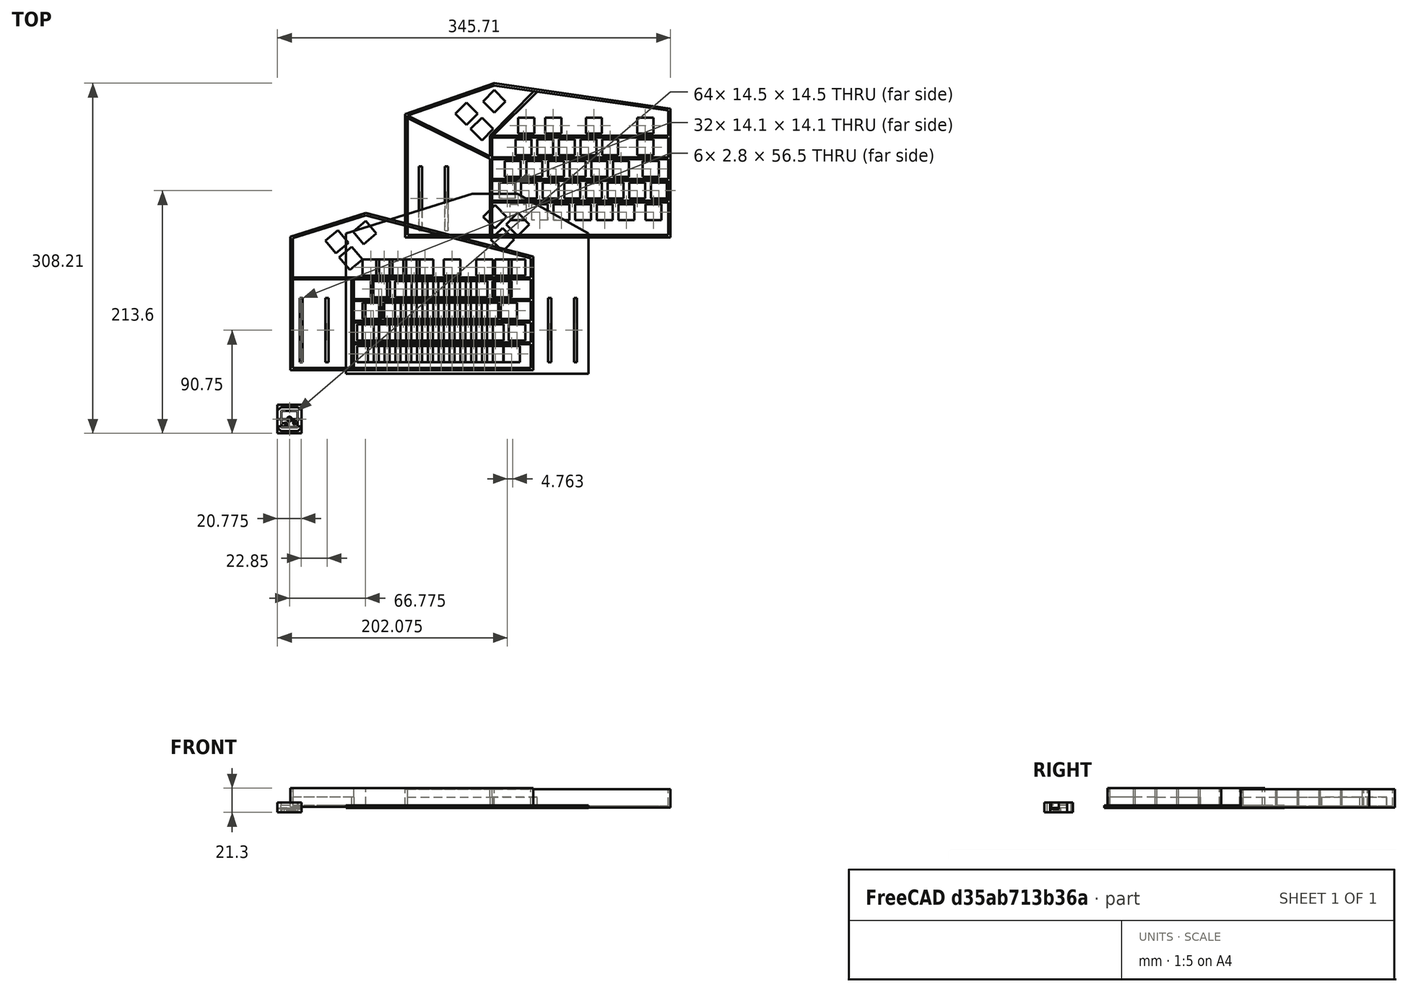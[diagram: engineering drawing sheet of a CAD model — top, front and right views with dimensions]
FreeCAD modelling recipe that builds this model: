
FCSTD DOCUMENT  (FreeCAD 0.22R35869 (Git))
Label: keyboard.FCStd.bak
License: All rights reserved
LicenseURL: http://en.wikipedia.org/wiki/All_rights_reserved
objects: Sketcher::SketchObject×30, PartDesign::Pad×30, PartDesign::Pocket×25, PartDesign::CoordinateSystem×11, PartDesign::Body×7, Part::Feature×6, App::Part×4, App::DocumentObjectGroup×3, App::Link×3, Mesh::Feature×3, Part::Refine×3, PartDesign::FeatureBase×3, PartDesign::Chamfer×2, PartDesign::Fillet×2, PartDesign::LinearPattern×2, App::FeaturePython×1, Spreadsheet::Sheet×1
note: 180 computed .brp shape members not serialized (recipe doc carries the construction recipe); baked Part::Feature solids carry a one-line shape summary decoded from their .brp

FEATURE [Sketcher::SketchObject] Sketch
  FullyConstrained = true
  MapMode = 5
  Support = -> [XY_Plane001]
  sketch-geometry (8):
    g0: LineSegment StartX=-7.5 StartY=7.5 StartZ=0 EndX=7.5 EndY=7.5 EndZ=0
    g1: LineSegment StartX=7.5 StartY=7.5 StartZ=0 EndX=7.5 EndY=-7.5 EndZ=0
    g2: LineSegment StartX=7.5 StartY=-7.5 StartZ=0 EndX=-7.5 EndY=-7.5 EndZ=0
    g3: LineSegment StartX=-7.5 StartY=-7.5 StartZ=0 EndX=-7.5 EndY=7.5 EndZ=0
    g4: LineSegment StartX=-10.5 StartY=10.5 StartZ=0 EndX=10.5 EndY=10.5 EndZ=0
    g5: LineSegment StartX=10.5 StartY=10.5 StartZ=0 EndX=10.5 EndY=-10.5 EndZ=0
    g6: LineSegment StartX=10.5 StartY=-10.5 StartZ=0 EndX=-10.5 EndY=-10.5 EndZ=0
    g7: LineSegment StartX=-10.5 StartY=-10.5 StartZ=0 EndX=-10.5 EndY=10.5 EndZ=0
  constraints (20):
    c: Coincident(g0,g1)
    c: Coincident(g1,g2)
    c: Coincident(g2,g3)
    c: Coincident(g3,g0)
    c: Horizontal(g2)
    c: Vertical(g1)
    c: Symmetric(g0,g0,g-2)
    c: Symmetric(g0,g2,g-1)
    c: Equal(g0,g3)
    c: DistanceX(g0,g0) = 15
    c: Coincident(g4,g5)
    c: Coincident(g5,g6)
    c: Coincident(g6,g7)
    c: Coincident(g7,g4)
    c: Horizontal(g6)
    c: Vertical(g5)
    c: Symmetric(g4,g4,g-2)
    c: Symmetric(g4,g6,g-1)
    c: Equal(g4,g7)
    c: DistanceX(g4,g0) = 3
FEATURE [PartDesign::Pad] Pad
  Direction = (0,0,1)
  Length = 2.5
  Length2 = 10
  Profile = -> Sketch
  ReferenceAxis = -> Sketch [N_Axis]
  Type = 0
FEATURE [Sketcher::SketchObject] Sketch001
  ExternalGeometry = -> [Pad]
  FullyConstrained = true
  MapMode = 5
  Placement = pos=(0,0,0) rot=(1,0,0;3.14159rad)
  Support = -> [Pad]
  expr: Constraints[11] = 4.15 / 2
  sketch-geometry (5):
    g0: LineSegment StartX=-10.5 StartY=10.5 StartZ=0 EndX=10.5 EndY=10.5 EndZ=0
    g1: LineSegment StartX=10.5 StartY=10.5 StartZ=0 EndX=10.5 EndY=-10.5 EndZ=0
    g2: LineSegment StartX=10.5 StartY=-10.5 StartZ=0 EndX=-10.5 EndY=-10.5 EndZ=0
    g3: LineSegment StartX=-10.5 StartY=-10.5 StartZ=0 EndX=-10.5 EndY=10.5 EndZ=0
    g4: Circle CenterX=0 CenterY=0 CenterZ=0 NormalX=0 NormalY=0 NormalZ=1 AngleXU=0 Radius=2.075
  constraints (12):
    c: Coincident(g0,g1)
    c: Coincident(g1,g2)
    c: Coincident(g2,g3)
    c: Coincident(g3,g0)
    c: Horizontal(g0)
    c: Horizontal(g2)
    c: Vertical(g1)
    c: Vertical(g3)
    c: Coincident(g0,g-3)
    c: Coincident(g1,g-4)
    c: Coincident(g4,g-1)
    c: Radius(g4) = 2.075
FEATURE [PartDesign::Pad] Pad001
  BaseFeature = -> Pad
  Direction = (0,0,-1)
  Length = 4
  Length2 = 10
  Profile = -> Sketch001
  ReferenceAxis = -> Sketch001 [N_Axis]
  Type = 0
FEATURE [Sketcher::SketchObject] Sketch002
  ExternalGeometry = -> [Pad001]
  FullyConstrained = true
  MapMode = 5
  Placement = pos=(0,0,2.5) rot=(0,0,1;0rad)
  Support = -> [Pad001]
  sketch-geometry (8):
    g0: LineSegment StartX=-10.5 StartY=10.5 StartZ=0 EndX=10.5 EndY=10.5 EndZ=0
    g1: LineSegment StartX=10.5 StartY=10.5 StartZ=0 EndX=10.5 EndY=-10.5 EndZ=0
    g2: LineSegment StartX=10.5 StartY=-10.5 StartZ=0 EndX=-10.5 EndY=-10.5 EndZ=0
    g3: LineSegment StartX=-10.5 StartY=-10.5 StartZ=0 EndX=-10.5 EndY=10.5 EndZ=0
    g4: LineSegment StartX=-7.25 StartY=7.25 StartZ=0 EndX=7.25 EndY=7.25 EndZ=0
    g5: LineSegment StartX=7.25 StartY=7.25 StartZ=0 EndX=7.25 EndY=-7.25 EndZ=0
    g6: LineSegment StartX=7.25 StartY=-7.25 StartZ=0 EndX=-7.25 EndY=-7.25 EndZ=0
    g7: LineSegment StartX=-7.25 StartY=-7.25 StartZ=0 EndX=-7.25 EndY=7.25 EndZ=0
  constraints (20):
    c: Coincident(g0,g1)
    c: Coincident(g1,g2)
    c: Coincident(g2,g3)
    c: Coincident(g3,g0)
    c: Horizontal(g0)
    c: Horizontal(g2)
    c: Vertical(g1)
    c: Vertical(g3)
    c: Coincident(g0,g-3)
    c: Coincident(g1,g-4)
    c: Coincident(g4,g5)
    c: Coincident(g5,g6)
    c: Coincident(g6,g7)
    c: Coincident(g7,g4)
    c: Horizontal(g6)
    c: Vertical(g5)
    c: Symmetric(g4,g4,g-2)
    c: Symmetric(g4,g6,g-1)
    c: DistanceX(g4,g4) = 14.5
    c: Equal(g7,g4)
FEATURE [PartDesign::Pad] Pad002
  BaseFeature = -> Pad001
  Direction = (0,0,1)
  Length = 2.3
  Length2 = 10
  Profile = -> Sketch002
  ReferenceAxis = -> Sketch002 [N_Axis]
  Type = 0
FEATURE [PartDesign::Chamfer] Chamfer
  Angle = 45
  Base = -> Pad002 [Edge19,Edge23,Edge11,Edge12]
  BaseFeature = -> Pad002
  ChamferType = 0
  FlipDirection = false
  Size = 3
  Size2 = 1
  SupportTransform = false
  UseAllEdges = false
FEATURE [Sketcher::SketchObject] Sketch003
  FullyConstrained = true
  MapMode = 5
  Placement = pos=(0,0,-4) rot=(1,0,0;3.14159rad)
  Support = -> [Chamfer]
  sketch-geometry (2):
    g0: Circle CenterX=4 CenterY=2.85 CenterZ=0 NormalX=0 NormalY=0 NormalZ=1 AngleXU=0 Radius=0.75
    g1: Circle CenterX=-2.9 CenterY=5 CenterZ=0 NormalX=0 NormalY=0 NormalZ=1 AngleXU=0 Radius=0.75
  constraints (6):
    c: DistanceX(g-1,g0) = 4
    c: DistanceY(g-1,g0) = 2.85
    c: Radius(g0) = 0.75
    c: DistanceX(g1,g-1) = 2.9
    c: DistanceY(g-1,g1) = 5
    c: Equal(g1,g0)
FEATURE [PartDesign::Pocket] Pocket
  BaseFeature = -> Chamfer
  Direction = (0,0,1)
  Length = 5
  Length2 = 5
  Profile = -> Sketch003
  ReferenceAxis = -> Sketch003 [N_Axis]
  Type = 1
FEATURE [PartDesign::Chamfer] Chamfer001
  Angle = 45
  Base = -> Pocket [Edge27,Edge26]
  BaseFeature = -> Pocket
  ChamferType = 1
  FlipDirection = false
  Size = 1.8
  Size2 = 3.999
  SupportTransform = false
  UseAllEdges = false
FEATURE [PartDesign::Body] Body
  Group = -> [Sketch,Pad,Sketch001,Pad001,Sketch002,Pad002,Chamfer,Sketch003,Pocket,Chamfer001]
  Origin = -> Origin001
  Tip = -> Chamfer001
FEATURE [Sketcher::SketchObject] Sketch004
  FullyConstrained = true
  MapMode = 5
  Support = -> [XY_Plane002]
  sketch-geometry (8):
    g0: LineSegment StartX=-7.5 StartY=7.5 StartZ=0 EndX=7.5 EndY=7.5 EndZ=0
    g1: LineSegment StartX=7.5 StartY=7.5 StartZ=0 EndX=7.5 EndY=-7.5 EndZ=0
    g2: LineSegment StartX=7.5 StartY=-7.5 StartZ=0 EndX=-7.5 EndY=-7.5 EndZ=0
    g3: LineSegment StartX=-7.5 StartY=-7.5 StartZ=0 EndX=-7.5 EndY=7.5 EndZ=0
    g4: LineSegment StartX=-10.5 StartY=10.5 StartZ=0 EndX=10.5 EndY=10.5 EndZ=0
    g5: LineSegment StartX=10.5 StartY=10.5 StartZ=0 EndX=10.5 EndY=-10.5 EndZ=0
    g6: LineSegment StartX=10.5 StartY=-10.5 StartZ=0 EndX=-10.5 EndY=-10.5 EndZ=0
    g7: LineSegment StartX=-10.5 StartY=-10.5 StartZ=0 EndX=-10.5 EndY=10.5 EndZ=0
  constraints (20):
    c: Coincident(g0,g1)
    c: Coincident(g1,g2)
    c: Coincident(g2,g3)
    c: Coincident(g3,g0)
    c: Horizontal(g2)
    c: Vertical(g1)
    c: Symmetric(g0,g0,g-2)
    c: Symmetric(g0,g2,g-1)
    c: Equal(g0,g3)
    c: DistanceX(g0,g0) = 15
    c: Coincident(g4,g5)
    c: Coincident(g5,g6)
    c: Coincident(g6,g7)
    c: Coincident(g7,g4)
    c: Horizontal(g6)
    c: Vertical(g5)
    c: Symmetric(g4,g4,g-2)
    c: Symmetric(g4,g6,g-1)
    c: Equal(g4,g7)
    c: DistanceX(g4,g0) = 3
FEATURE [PartDesign::Pad] Pad003
  Direction = (0,0,1)
  Length = 2.5
  Length2 = 10
  Profile = -> Sketch004
  ReferenceAxis = -> Sketch004 [N_Axis]
  Type = 0
FEATURE [Sketcher::SketchObject] Sketch005
  ExternalGeometry = -> [Pad003]
  FullyConstrained = true
  MapMode = 5
  Placement = pos=(0,0,0) rot=(1,0,0;3.14159rad)
  Support = -> [Pad003]
  expr: Constraints[11] = 4.15 / 2
  sketch-geometry (5):
    g0: LineSegment StartX=-10.5 StartY=10.5 StartZ=0 EndX=10.5 EndY=10.5 EndZ=0
    g1: LineSegment StartX=10.5 StartY=10.5 StartZ=0 EndX=10.5 EndY=-10.5 EndZ=0
    g2: LineSegment StartX=10.5 StartY=-10.5 StartZ=0 EndX=-10.5 EndY=-10.5 EndZ=0
    g3: LineSegment StartX=-10.5 StartY=-10.5 StartZ=0 EndX=-10.5 EndY=10.5 EndZ=0
    g4: Circle CenterX=0 CenterY=0 CenterZ=0 NormalX=0 NormalY=0 NormalZ=1 AngleXU=0 Radius=2.075
  constraints (12):
    c: Coincident(g0,g1)
    c: Coincident(g1,g2)
    c: Coincident(g2,g3)
    c: Coincident(g3,g0)
    c: Horizontal(g0)
    c: Horizontal(g2)
    c: Vertical(g1)
    c: Vertical(g3)
    c: Coincident(g0,g-3)
    c: Coincident(g1,g-4)
    c: Coincident(g4,g-1)
    c: Radius(g4) = 2.075
FEATURE [PartDesign::Pad] Pad004
  BaseFeature = -> Pad003
  Direction = (0,0,-1)
  Length = 4
  Length2 = 10
  Profile = -> Sketch005
  ReferenceAxis = -> Sketch005 [N_Axis]
  Type = 0
FEATURE [Sketcher::SketchObject] Sketch006
  ExternalGeometry = -> [Pad004]
  FullyConstrained = true
  MapMode = 5
  Placement = pos=(0,0,2.5) rot=(0,0,1;0rad)
  Support = -> [Pad004]
  sketch-geometry (8):
    g0: LineSegment StartX=-10.5 StartY=10.5 StartZ=0 EndX=10.5 EndY=10.5 EndZ=0
    g1: LineSegment StartX=10.5 StartY=10.5 StartZ=0 EndX=10.5 EndY=-10.5 EndZ=0
    g2: LineSegment StartX=10.5 StartY=-10.5 StartZ=0 EndX=-10.5 EndY=-10.5 EndZ=0
    g3: LineSegment StartX=-10.5 StartY=-10.5 StartZ=0 EndX=-10.5 EndY=10.5 EndZ=0
    g4: LineSegment StartX=-7.25 StartY=7.25 StartZ=0 EndX=7.25 EndY=7.25 EndZ=0
    g5: LineSegment StartX=7.25 StartY=7.25 StartZ=0 EndX=7.25 EndY=-7.25 EndZ=0
    g6: LineSegment StartX=7.25 StartY=-7.25 StartZ=0 EndX=-7.25 EndY=-7.25 EndZ=0
    g7: LineSegment StartX=-7.25 StartY=-7.25 StartZ=0 EndX=-7.25 EndY=7.25 EndZ=0
  constraints (20):
    c: Coincident(g0,g1)
    c: Coincident(g1,g2)
    c: Coincident(g2,g3)
    c: Coincident(g3,g0)
    c: Horizontal(g0)
    c: Horizontal(g2)
    c: Vertical(g1)
    c: Vertical(g3)
    c: Coincident(g0,g-3)
    c: Coincident(g1,g-4)
    c: Coincident(g4,g5)
    c: Coincident(g5,g6)
    c: Coincident(g6,g7)
    c: Coincident(g7,g4)
    c: Horizontal(g6)
    c: Vertical(g5)
    c: Symmetric(g4,g4,g-2)
    c: Symmetric(g4,g6,g-1)
    c: DistanceX(g4,g4) = 14.5
    c: Equal(g7,g4)
FEATURE [PartDesign::Pad] Pad005
  BaseFeature = -> Pad004
  Direction = (0,0,1)
  Length = 2.3
  Length2 = 10
  Profile = -> Sketch006
  ReferenceAxis = -> Sketch006 [N_Axis]
  Type = 0
FEATURE [Sketcher::SketchObject] Sketch007
  ExternalGeometry = -> [Pad005]
  FullyConstrained = true
  MapMode = 5
  Placement = pos=(0,0,-4) rot=(1,0,0;3.14159rad)
  Support = -> [Pad005]
  sketch-geometry (22):
    g0: LineSegment StartX=-7.5 StartY=6.5 StartZ=0 EndX=-2 EndY=6.5 EndZ=0
    g1: LineSegment StartX=-2 StartY=6.5 StartZ=0 EndX=-2 EndY=3.5 EndZ=0
    g2: LineSegment StartX=-2 StartY=3.5 StartZ=0 EndX=-7.5 EndY=3.5 EndZ=0
    g3: LineSegment StartX=-7.5 StartY=3.5 StartZ=0 EndX=-7.5 EndY=6.5 EndZ=0
    g4: LineSegment StartX=3 StartY=4.35 StartZ=0 EndX=7.5 EndY=4.35 EndZ=0
    g5: LineSegment StartX=7.5 StartY=4.35 StartZ=0 EndX=7.5 EndY=1.35 EndZ=0
    g6: LineSegment StartX=7.5 StartY=1.35 StartZ=0 EndX=3 EndY=1.35 EndZ=0
    g7: LineSegment StartX=3 StartY=1.35 StartZ=0 EndX=3 EndY=4.35 EndZ=0
    g8: Circle CenterX=-2.9 CenterY=5 CenterZ=0 NormalX=0 NormalY=0 NormalZ=1 AngleXU=0 Radius=0.75
    g9: Circle CenterX=4 CenterY=2.85 CenterZ=0 NormalX=0 NormalY=0 NormalZ=1 AngleXU=0 Radius=0.75
    g10: LineSegment StartX=-2.9 StartY=5 StartZ=0 EndX=-7.5 EndY=5 EndZ=0
    g11: LineSegment StartX=-7.5 StartY=5 StartZ=0 EndX=-7.5 EndY=6.5 EndZ=0
    g12: LineSegment StartX=-7.5 StartY=5 StartZ=0 EndX=-7.5 EndY=3.5 EndZ=0
    g13: LineSegment StartX=4 StartY=2.85 StartZ=0 EndX=7.5 EndY=2.85 EndZ=0
    g14: LineSegment StartX=7.5 StartY=2.85 StartZ=0 EndX=7.5 EndY=1.35 EndZ=0
    g15: LineSegment StartX=7.5 StartY=2.85 StartZ=0 EndX=7.5 EndY=4.35 EndZ=0
    g16: LineSegment StartX=3 StartY=4.35 StartZ=0 EndX=3.8 EndY=3.57284 EndZ=0
    g17: LineSegment StartX=3 StartY=1.35 StartZ=0 EndX=3.8 EndY=2.12716 EndZ=0
    g18: ArcOfCircle CenterX=4 CenterY=2.85 CenterZ=0 NormalX=0 NormalY=0 NormalZ=1 AngleXU=0 Radius=0.75 StartAngle=1.84073 EndAngle=4.44246
    g19: LineSegment StartX=-2 StartY=6.5 StartZ=0 EndX=-2.7 EndY=5.72284 EndZ=0
    g20: LineSegment StartX=-2 StartY=3.5 StartZ=0 EndX=-2.7 EndY=4.27716 EndZ=0
    g21: ArcOfCircle CenterX=-2.9 CenterY=5 CenterZ=0 NormalX=0 NormalY=0 NormalZ=1 AngleXU=0 Radius=0.75 StartAngle=4.98232 EndAngle=7.58405
  constraints (60):
    c: Coincident(g0,g1)
    c: Coincident(g1,g2)
    c: Coincident(g2,g3)
    c: Coincident(g3,g0)
    c: Horizontal(g0)
    c: Horizontal(g2)
    c: Vertical(g1)
    c: Vertical(g3)
    c: Coincident(g4,g5)
    c: Coincident(g5,g6)
    c: Coincident(g6,g7)
    c: Coincident(g7,g4)
    c: Horizontal(g4)
    c: Horizontal(g6)
    c: Vertical(g5)
    c: Vertical(g7)
    c: PointOnObject(g4,g-4)
    c: PointOnObject(g0,g-3)
    c: DistanceY(g-1,g9) = 2.85
    c: DistanceX(g-1,g9) = 4
    c: Radius(g9) = 0.75
    c: DistanceY(g-1,g8) = 5
    c: DistanceX(g8,g-1) = 2.9
    c: Radius(g8) = 0.75
    c: Coincident(g10,g8)
    c: PointOnObject(g10,g-3)
    c: Coincident(g11,g10)
    c: Equal(g12,g11)
    c: Coincident(g12,g10)
    c: Horizontal(g10)
    c: Coincident(g12,g2)
    c: Coincident(g11,g0)
    c: Coincident(g13,g9)
    c: PointOnObject(g13,g-4)
    c: Coincident(g14,g13)
    c: Coincident(g15,g13)
    c: Equal(g15,g14)
    c: Horizontal(g13)
    c: Coincident(g15,g4)
    c: Coincident(g14,g5)
    c: DistanceX(g6,g5) = 4.5
    c: DistanceX(g2,g2) = 5.5
    c: DistanceY(g1,g1) = 3
    c: Coincident(g16,g4)
    c: Coincident(g17,g6)
    c: Coincident(g18,g9)
    c: Coincident(g18,g16)
    c: Coincident(g18,g17)
    c: Equal(g18,g9)
    c: DistanceX(g17,g18) = 0.2
    c: Equal(g16,g17)
    c: Coincident(g19,g0)
    c: PointOnObject(g19,g8)
    c: Coincident(g20,g2)
    c: Coincident(g21,g8)
    c: Coincident(g21,g19)
    c: Coincident(g21,g20)
    c: Equal(g19,g20)
    c: DistanceX(g21,g20) = 0.2
    c: Equal(g1,g7)
FEATURE [PartDesign::Pocket] Pocket001
  BaseFeature = -> Pad005
  Direction = (0,0,1)
  Length = 0
  Length2 = 5
  Profile = -> Sketch007
  ReferenceAxis = -> Sketch007 [N_Axis]
  Type = 3
  UpToFace = -> Pad005 [Face20]
FEATURE [PartDesign::Fillet] Fillet
  Base = -> Pocket001 [Edge65,Edge68,Edge49,Edge53]
  BaseFeature = -> Pocket001
  Radius = 1
  SupportTransform = false
  UseAllEdges = false
FEATURE [Sketcher::SketchObject] Sketch008
  ExternalGeometry = -> [Fillet]
  FullyConstrained = true
  MapMode = 5
  Placement = pos=(0,0,4.8) rot=(0,0,1;0rad)
  Support = -> [Fillet]
  sketch-geometry (4):
    g0: LineSegment StartX=-10.5 StartY=0 StartZ=0 EndX=10.5 EndY=0 EndZ=0
    g1: LineSegment StartX=10.5 StartY=0 StartZ=0 EndX=10.5 EndY=-6.5 EndZ=0
    g2: LineSegment StartX=10.5 StartY=-6.5 StartZ=0 EndX=-10.5 EndY=-6.5 EndZ=0
    g3: LineSegment StartX=-10.5 StartY=-6.5 StartZ=0 EndX=-10.5 EndY=0 EndZ=0
  constraints (11):
    c: Coincident(g0,g1)
    c: Coincident(g1,g2)
    c: Coincident(g2,g3)
    c: Coincident(g3,g0)
    c: Horizontal(g2)
    c: Vertical(g1)
    c: Vertical(g3)
    c: PointOnObject(g0,g-1)
    c: PointOnObject(g2,g-3)
    c: Symmetric(g0,g0,g-2)
    c: PointOnObject(g2,g-4)
FEATURE [PartDesign::Pocket] Pocket002
  BaseFeature = -> Fillet
  Direction = (0,0,-1)
  Length = 0
  Length2 = 5
  Profile = -> Sketch008
  ReferenceAxis = -> Sketch008 [N_Axis]
  Type = 3
  UpToFace = -> Fillet [Face23]
FEATURE [PartDesign::Pad] Pad006
  BaseFeature = -> Pocket002
  Direction = (0,-1,0)
  Length = 2
  Length2 = 10
  Profile = -> Pocket002 [Face10,Face26,Face39]
  Type = 0
FEATURE [PartDesign::Pad] Pad007
  BaseFeature = -> Pad006
  Direction = (0,1,0)
  Length = 2
  Length2 = 10
  Profile = -> Pad006 [Face13,Face34,Face50]
  Type = 0
FEATURE [PartDesign::CoordinateSystem] LCS_Origin
  AttacherType = Attacher::AttachEngine3D
  MapMode = 2
  Support = -> [X_Axis006]
FEATURE [App::DocumentObjectGroup] Constraints
FEATURE [App::FeaturePython] Variables  # WARN: FeaturePython — macro-defined, semantics opaque (R4)
  Type = App::PropertyContainer
FEATURE [App::DocumentObjectGroup] Configurations
FEATURE [PartDesign::CoordinateSystem] LCS_0
  AttacherType = Attacher::AttachEngine3D
  MapMode = 2
  Support = -> [X_Axis007]
FEATURE [Sketcher::SketchObject] Sketch013
  FullyConstrained = true
  MapMode = 5
  Support = -> [XY_Plane008]
  sketch-geometry (6):
    g0: ArcOfCircle CenterX=-0.866025 CenterY=0 CenterZ=0 NormalX=0 NormalY=0 NormalZ=1 AngleXU=0 Radius=1 StartAngle=5.75959 EndAngle=6.80678
    g1: LineSegment StartX=0 StartY=0.5 StartZ=0 EndX=0 EndY=1 EndZ=0
    g2: LineSegment StartX=0 StartY=1 StartZ=0 EndX=1 EndY=1 EndZ=0
    g3: LineSegment StartX=1 StartY=1 StartZ=0 EndX=1 EndY=-1 EndZ=0
    g4: LineSegment StartX=1 StartY=-1 StartZ=0 EndX=0 EndY=-1 EndZ=0
    g5: LineSegment StartX=0 StartY=-1 StartZ=0 EndX=2e-16 EndY=-0.5 EndZ=0
  constraints (19):
    c: PointOnObject(g0,g-1)
    c: PointOnObject(g0,g-2)
    c: PointOnObject(g0,g-2)
    c: Coincident(g1,g2)
    c: Horizontal(g2)
    c: Coincident(g2,g3)
    c: Coincident(g3,g4)
    c: PointOnObject(g4,g-2)
    c: Horizontal(g4)
    c: Coincident(g4,g5)
    c: Coincident(g5,g0)
    c: PointOnObject(g1,g-2)
    c: Vertical(g3)
    c: DistanceY(g3,g3) = 2
    c: Radius(g0) = 1
    c: Coincident(g1,g0)
    c: Equal(g1,g5)
    c: DistanceY(g0,g0) = 1
    c: DistanceX(g2,g2) = 1
FEATURE [PartDesign::Pad] Pad011
  Direction = (0,0,1)
  Length = 4
  Length2 = 10
  Profile = -> Sketch013
  ReferenceAxis = -> Sketch013 [N_Axis]
  Reversed = true
  Type = 0
FEATURE [PartDesign::CoordinateSystem] Local_CS
  AttacherType = Attacher::AttachEngine3D
  MapMode = 45
  Placement = pos=(3.31163,-2.85,0) rot=(0,0.707107,0.707107;3.14159rad)
  Support = -> [Pad007]
FEATURE [PartDesign::CoordinateSystem] Local_CS001
  AttacherType = Attacher::AttachEngine3D
  MapMode = 45
  Placement = pos=(-2.22398,-5,0) rot=(0,0.707107,0.707107;3.14159rad)
  Support = -> [Pad007]
FEATURE [PartDesign::Body] Body001
  Group = -> [Sketch004,Pad003,Sketch005,Pad004,Sketch006,Pad005,Sketch007,Pocket001,Fillet,Sketch008,Pocket002,Pad006,Pad007,Local_CS,Local_CS001]
  Origin = -> Origin002
  Tip = -> Pad007
FEATURE [Sketcher::SketchObject] Sketch014
  ExternalGeometry = -> [Pad011]
  FullyConstrained = true
  MapMode = 5
  Support = -> [XY_Plane008]
  sketch-geometry (21):
    g0: LineSegment StartX=1 StartY=1 StartZ=0 EndX=1.66667 EndY=-0.8 EndZ=0
    g1: LineSegment StartX=1.66667 StartY=-0.8 StartZ=0 EndX=2.33333 EndY=1 EndZ=0
    g2: LineSegment StartX=2.33333 StartY=1 StartZ=0 EndX=3 EndY=-0.8 EndZ=0
    g3: LineSegment StartX=3 StartY=-0.8 StartZ=0 EndX=3.66667 EndY=1 EndZ=0
    g4: LineSegment StartX=3.66667 StartY=1 StartZ=0 EndX=4.33333 EndY=-0.8 EndZ=0
    g5: LineSegment StartX=4.33333 StartY=-0.8 StartZ=0 EndX=5 EndY=1 EndZ=0
    g6: LineSegment StartX=1 StartY=1 StartZ=0 EndX=5 EndY=1 EndZ=0
    g7: LineSegment StartX=1 StartY=-1 StartZ=0 EndX=4.33333 EndY=-1 EndZ=0
    g8: LineSegment StartX=1 StartY=0.8 StartZ=0 EndX=1.66667 EndY=-1 EndZ=0
    g9: LineSegment StartX=1.66667 StartY=-1 StartZ=0 EndX=2.33333 EndY=0.8 EndZ=0
    g10: LineSegment StartX=2.33333 StartY=0.8 StartZ=0 EndX=3 EndY=-1 EndZ=0
    g11: LineSegment StartX=3 StartY=-1 StartZ=0 EndX=3.66667 EndY=0.8 EndZ=0
    g12: LineSegment StartX=3.66667 StartY=0.8 StartZ=0 EndX=4.33333 EndY=-1 EndZ=0
    g13: LineSegment StartX=4.33333 StartY=-1 StartZ=0 EndX=5 EndY=0.8 EndZ=0
    g14: LineSegment StartX=1.66667 StartY=-0.8 StartZ=0 EndX=1.66667 EndY=-1 EndZ=0
    g15: LineSegment StartX=3 StartY=-0.8 StartZ=0 EndX=3 EndY=-1 EndZ=0
    g16: LineSegment StartX=2.33333 StartY=0.8 StartZ=0 EndX=2.33333 EndY=1 EndZ=0
    g17: LineSegment StartX=3.66667 StartY=0.8 StartZ=0 EndX=3.66667 EndY=1 EndZ=0
    g18: LineSegment StartX=5 StartY=0.8 StartZ=0 EndX=5 EndY=1 EndZ=0
    g19: LineSegment StartX=4.33333 StartY=-0.8 StartZ=0 EndX=4.33333 EndY=-1 EndZ=0
    g20: LineSegment StartX=1 StartY=0.8 StartZ=0 EndX=1 EndY=1 EndZ=0
  constraints (55):
    c: Coincident(g-3,g0)
    c: Coincident(g0,g1)
    c: Coincident(g1,g2)
    c: Coincident(g2,g3)
    c: Coincident(g3,g4)
    c: Coincident(g6,g0)
    c: Coincident(g6,g5)
    c: Coincident(g7,g-3)
    c: Horizontal(g7)
    c: Horizontal(g6)
    c: PointOnObject(g3,g6)
    c: PointOnObject(g1,g6)
    c: Coincident(g5,g4)
    c: PointOnObject(g8,g-3)
    c: PointOnObject(g8,g7)
    c: Coincident(g8,g9)
    c: Coincident(g9,g10)
    c: PointOnObject(g10,g7)
    c: Coincident(g10,g11)
    c: Coincident(g11,g12)
    c: Coincident(g12,g7)
    c: Coincident(g12,g13)
    c: Coincident(g14,g0)
    c: Coincident(g14,g8)
    c: Coincident(g15,g2)
    c: Coincident(g15,g10)
    c: Coincident(g16,g9)
    c: Coincident(g16,g1)
    c: Coincident(g17,g11)
    c: Coincident(g17,g3)
    c: Vertical(g17)
    c: Coincident(g18,g13)
    c: Coincident(g18,g5)
    c: Coincident(g19,g4)
    c: Coincident(g19,g12)
    c: Equal(g14,g16)
    c: Equal(g16,g15)
    c: Equal(g15,g17)
    c: Equal(g17,g19)
    c: Equal(g19,g18)
    c: Vertical(g14)
    c: Vertical(g16)
    c: Vertical(g15)
    c: Vertical(g18)
    c: Vertical(g19)
    c: Equal(g0,g1)
    c: Equal(g2,g3)
    c: Equal(g3,g4)
    c: Equal(g4,g5)
    c: Equal(g5,g8)
    c: Equal(g8,g9)
    c: Coincident(g20,g8)
    c: Coincident(g20,g0)
    c: DistanceY(g18,g18) = 0.2
    c: DistanceX(g6,g6) = 4
FEATURE [PartDesign::Pad] Pad012
  BaseFeature = -> Pad011
  Direction = (0,0,1)
  Length = 4
  Length2 = 10
  Profile = -> Sketch014
  ReferenceAxis = -> Sketch014 [N_Axis]
  Reversed = true
  Type = 0
FEATURE [PartDesign::CoordinateSystem] LCS_0002
  AttacherType = Attacher::AttachEngine3D
  MapMode = 2
  Support = -> [X_Axis009]
FEATURE [Sketcher::SketchObject] Sketch015
  FullyConstrained = true
  MapMode = 5
  Support = -> [XY_Plane010]
  sketch-geometry (8):
    g0: LineSegment StartX=-7.5 StartY=7.5 StartZ=0 EndX=7.5 EndY=7.5 EndZ=0
    g1: LineSegment StartX=7.5 StartY=7.5 StartZ=0 EndX=7.5 EndY=-7.5 EndZ=0
    g2: LineSegment StartX=7.5 StartY=-7.5 StartZ=0 EndX=-7.5 EndY=-7.5 EndZ=0
    g3: LineSegment StartX=-7.5 StartY=-7.5 StartZ=0 EndX=-7.5 EndY=7.5 EndZ=0
    g4: LineSegment StartX=-10.5 StartY=10.5 StartZ=0 EndX=10.5 EndY=10.5 EndZ=0
    g5: LineSegment StartX=10.5 StartY=10.5 StartZ=0 EndX=10.5 EndY=-10.5 EndZ=0
    g6: LineSegment StartX=10.5 StartY=-10.5 StartZ=0 EndX=-10.5 EndY=-10.5 EndZ=0
    g7: LineSegment StartX=-10.5 StartY=-10.5 StartZ=0 EndX=-10.5 EndY=10.5 EndZ=0
  constraints (20):
    c: Coincident(g0,g1)
    c: Coincident(g1,g2)
    c: Coincident(g2,g3)
    c: Coincident(g3,g0)
    c: Horizontal(g2)
    c: Vertical(g1)
    c: Symmetric(g0,g0,g-2)
    c: Symmetric(g0,g2,g-1)
    c: Equal(g0,g3)
    c: DistanceX(g0,g0) = 15
    c: Coincident(g4,g5)
    c: Coincident(g5,g6)
    c: Coincident(g6,g7)
    c: Coincident(g7,g4)
    c: Horizontal(g6)
    c: Vertical(g5)
    c: Symmetric(g4,g4,g-2)
    c: Symmetric(g4,g6,g-1)
    c: Equal(g4,g7)
    c: DistanceX(g4,g0) = 3
FEATURE [PartDesign::Pad] Pad013
  Direction = (0,0,1)
  Length = 2.5
  Length2 = 10
  Profile = -> Sketch015
  ReferenceAxis = -> Sketch015 [N_Axis]
  Type = 0
FEATURE [Sketcher::SketchObject] Sketch016
  ExternalGeometry = -> [Pad013]
  FullyConstrained = true
  MapMode = 5
  Placement = pos=(0,0,0) rot=(1,0,0;3.14159rad)
  Support = -> [Pad013]
  expr: Constraints[11] = 4.15 / 2
  sketch-geometry (5):
    g0: LineSegment StartX=-10.5 StartY=10.5 StartZ=0 EndX=10.5 EndY=10.5 EndZ=0
    g1: LineSegment StartX=10.5 StartY=10.5 StartZ=0 EndX=10.5 EndY=-10.5 EndZ=0
    g2: LineSegment StartX=10.5 StartY=-10.5 StartZ=0 EndX=-10.5 EndY=-10.5 EndZ=0
    g3: LineSegment StartX=-10.5 StartY=-10.5 StartZ=0 EndX=-10.5 EndY=10.5 EndZ=0
    g4: Circle CenterX=0 CenterY=0 CenterZ=0 NormalX=0 NormalY=0 NormalZ=1 AngleXU=0 Radius=2.075
  constraints (12):
    c: Coincident(g0,g1)
    c: Coincident(g1,g2)
    c: Coincident(g2,g3)
    c: Coincident(g3,g0)
    c: Horizontal(g0)
    c: Horizontal(g2)
    c: Vertical(g1)
    c: Vertical(g3)
    c: Coincident(g0,g-3)
    c: Coincident(g1,g-4)
    c: Coincident(g4,g-1)
    c: Radius(g4) = 2.075
FEATURE [PartDesign::Pad] Pad014
  BaseFeature = -> Pad013
  Direction = (0,0,-1)
  Length = 4
  Length2 = 10
  Profile = -> Sketch016
  ReferenceAxis = -> Sketch016 [N_Axis]
  Type = 0
FEATURE [Sketcher::SketchObject] Sketch017
  ExternalGeometry = -> [Pad014]
  FullyConstrained = true
  MapMode = 5
  Placement = pos=(0,0,2.5) rot=(0,0,1;0rad)
  Support = -> [Pad014]
  sketch-geometry (8):
    g0: LineSegment StartX=-10.5 StartY=10.5 StartZ=0 EndX=10.5 EndY=10.5 EndZ=0
    g1: LineSegment StartX=10.5 StartY=10.5 StartZ=0 EndX=10.5 EndY=-10.5 EndZ=0
    g2: LineSegment StartX=10.5 StartY=-10.5 StartZ=0 EndX=-10.5 EndY=-10.5 EndZ=0
    g3: LineSegment StartX=-10.5 StartY=-10.5 StartZ=0 EndX=-10.5 EndY=10.5 EndZ=0
    g4: LineSegment StartX=-7.25 StartY=7.25 StartZ=0 EndX=7.25 EndY=7.25 EndZ=0
    g5: LineSegment StartX=7.25 StartY=7.25 StartZ=0 EndX=7.25 EndY=-7.25 EndZ=0
    g6: LineSegment StartX=7.25 StartY=-7.25 StartZ=0 EndX=-7.25 EndY=-7.25 EndZ=0
    g7: LineSegment StartX=-7.25 StartY=-7.25 StartZ=0 EndX=-7.25 EndY=7.25 EndZ=0
  constraints (20):
    c: Coincident(g0,g1)
    c: Coincident(g1,g2)
    c: Coincident(g2,g3)
    c: Coincident(g3,g0)
    c: Horizontal(g0)
    c: Horizontal(g2)
    c: Vertical(g1)
    c: Vertical(g3)
    c: Coincident(g0,g-3)
    c: Coincident(g1,g-4)
    c: Coincident(g4,g5)
    c: Coincident(g5,g6)
    c: Coincident(g6,g7)
    c: Coincident(g7,g4)
    c: Horizontal(g6)
    c: Vertical(g5)
    c: Symmetric(g4,g4,g-2)
    c: Symmetric(g4,g6,g-1)
    c: DistanceX(g4,g4) = 14.5
    c: Equal(g7,g4)
FEATURE [PartDesign::Pad] Pad015
  BaseFeature = -> Pad014
  Direction = (0,0,1)
  Length = 2.3
  Length2 = 10
  Profile = -> Sketch017
  ReferenceAxis = -> Sketch017 [N_Axis]
  Type = 0
FEATURE [Sketcher::SketchObject] Sketch018
  ExternalGeometry = -> [Pad015]
  FullyConstrained = true
  MapMode = 5
  Placement = pos=(0,0,-4) rot=(1,0,0;3.14159rad)
  Support = -> [Pad015]
  sketch-geometry (22):
    g0: LineSegment StartX=-7.5 StartY=6.5 StartZ=0 EndX=-2 EndY=6.5 EndZ=0
    g1: LineSegment StartX=-2 StartY=6.5 StartZ=0 EndX=-2 EndY=3.5 EndZ=0
    g2: LineSegment StartX=-2 StartY=3.5 StartZ=0 EndX=-7.5 EndY=3.5 EndZ=0
    g3: LineSegment StartX=-7.5 StartY=3.5 StartZ=0 EndX=-7.5 EndY=6.5 EndZ=0
    g4: LineSegment StartX=3 StartY=4.35 StartZ=0 EndX=7.5 EndY=4.35 EndZ=0
    g5: LineSegment StartX=7.5 StartY=4.35 StartZ=0 EndX=7.5 EndY=1.35 EndZ=0
    g6: LineSegment StartX=7.5 StartY=1.35 StartZ=0 EndX=3 EndY=1.35 EndZ=0
    g7: LineSegment StartX=3 StartY=1.35 StartZ=0 EndX=3 EndY=4.35 EndZ=0
    g8: Circle CenterX=-2.9 CenterY=5 CenterZ=0 NormalX=0 NormalY=0 NormalZ=1 AngleXU=0 Radius=0.75
    g9: Circle CenterX=4 CenterY=2.85 CenterZ=0 NormalX=0 NormalY=0 NormalZ=1 AngleXU=0 Radius=0.75
    g10: LineSegment StartX=-2.9 StartY=5 StartZ=0 EndX=-7.5 EndY=5 EndZ=0
    g11: LineSegment StartX=-7.5 StartY=5 StartZ=0 EndX=-7.5 EndY=6.5 EndZ=0
    g12: LineSegment StartX=-7.5 StartY=5 StartZ=0 EndX=-7.5 EndY=3.5 EndZ=0
    g13: LineSegment StartX=4 StartY=2.85 StartZ=0 EndX=7.5 EndY=2.85 EndZ=0
    g14: LineSegment StartX=7.5 StartY=2.85 StartZ=0 EndX=7.5 EndY=1.35 EndZ=0
    g15: LineSegment StartX=7.5 StartY=2.85 StartZ=0 EndX=7.5 EndY=4.35 EndZ=0
    g16: LineSegment StartX=3 StartY=4.35 StartZ=0 EndX=3.8 EndY=3.57284 EndZ=0
    g17: LineSegment StartX=3 StartY=1.35 StartZ=0 EndX=3.8 EndY=2.12716 EndZ=0
    g18: ArcOfCircle CenterX=4 CenterY=2.85 CenterZ=0 NormalX=0 NormalY=0 NormalZ=1 AngleXU=0 Radius=0.75 StartAngle=1.84073 EndAngle=4.44246
    g19: LineSegment StartX=-2 StartY=6.5 StartZ=0 EndX=-2.7 EndY=5.72284 EndZ=0
    g20: LineSegment StartX=-2 StartY=3.5 StartZ=0 EndX=-2.7 EndY=4.27716 EndZ=0
    g21: ArcOfCircle CenterX=-2.9 CenterY=5 CenterZ=0 NormalX=0 NormalY=0 NormalZ=1 AngleXU=0 Radius=0.75 StartAngle=4.98232 EndAngle=7.58405
  constraints (60):
    c: Coincident(g0,g1)
    c: Coincident(g1,g2)
    c: Coincident(g2,g3)
    c: Coincident(g3,g0)
    c: Horizontal(g0)
    c: Horizontal(g2)
    c: Vertical(g1)
    c: Vertical(g3)
    c: Coincident(g4,g5)
    c: Coincident(g5,g6)
    c: Coincident(g6,g7)
    c: Coincident(g7,g4)
    c: Horizontal(g4)
    c: Horizontal(g6)
    c: Vertical(g5)
    c: Vertical(g7)
    c: PointOnObject(g4,g-4)
    c: PointOnObject(g0,g-3)
    c: DistanceY(g-1,g9) = 2.85
    c: DistanceX(g-1,g9) = 4
    c: Radius(g9) = 0.75
    c: DistanceY(g-1,g8) = 5
    c: DistanceX(g8,g-1) = 2.9
    c: Radius(g8) = 0.75
    c: Coincident(g10,g8)
    c: PointOnObject(g10,g-3)
    c: Coincident(g11,g10)
    c: Equal(g12,g11)
    c: Coincident(g12,g10)
    c: Horizontal(g10)
    c: Coincident(g12,g2)
    c: Coincident(g11,g0)
    c: Coincident(g13,g9)
    c: PointOnObject(g13,g-4)
    c: Coincident(g14,g13)
    c: Coincident(g15,g13)
    c: Equal(g15,g14)
    c: Horizontal(g13)
    c: Coincident(g15,g4)
    c: Coincident(g14,g5)
    c: DistanceX(g6,g5) = 4.5
    c: DistanceX(g2,g2) = 5.5
    c: DistanceY(g1,g1) = 3
    c: Coincident(g16,g4)
    c: Coincident(g17,g6)
    c: Coincident(g18,g9)
    c: Coincident(g18,g16)
    c: Coincident(g18,g17)
    c: Equal(g18,g9)
    c: DistanceX(g17,g18) = 0.2
    c: Equal(g16,g17)
    c: Coincident(g19,g0)
    c: PointOnObject(g19,g8)
    c: Coincident(g20,g2)
    c: Coincident(g21,g8)
    c: Coincident(g21,g19)
    c: Coincident(g21,g20)
    c: Equal(g19,g20)
    c: DistanceX(g21,g20) = 0.2
    c: Equal(g1,g7)
FEATURE [PartDesign::Pocket] Pocket003
  BaseFeature = -> Pad015
  Direction = (0,0,1)
  Length = 0
  Length2 = 5
  Profile = -> Sketch018
  ReferenceAxis = -> Sketch018 [N_Axis]
  Type = 3
  UpToFace = -> Pad015 [Face20]
FEATURE [PartDesign::Fillet] Fillet001
  Base = -> Pocket003 [Edge65,Edge68,Edge49,Edge53]
  BaseFeature = -> Pocket003
  Radius = 1
  SupportTransform = false
  UseAllEdges = false
FEATURE [Sketcher::SketchObject] Sketch019
  ExternalGeometry = -> [Fillet001]
  FullyConstrained = true
  MapMode = 5
  Placement = pos=(0,0,4.8) rot=(0,0,1;0rad)
  Support = -> [Fillet001]
  sketch-geometry (4):
    g0: LineSegment StartX=-10.5 StartY=0 StartZ=0 EndX=10.5 EndY=0 EndZ=0
    g1: LineSegment StartX=10.5 StartY=0 StartZ=0 EndX=10.5 EndY=-6.5 EndZ=0
    g2: LineSegment StartX=10.5 StartY=-6.5 StartZ=0 EndX=-10.5 EndY=-6.5 EndZ=0
    g3: LineSegment StartX=-10.5 StartY=-6.5 StartZ=0 EndX=-10.5 EndY=0 EndZ=0
  constraints (11):
    c: Coincident(g0,g1)
    c: Coincident(g1,g2)
    c: Coincident(g2,g3)
    c: Coincident(g3,g0)
    c: Horizontal(g2)
    c: Vertical(g1)
    c: Vertical(g3)
    c: PointOnObject(g0,g-1)
    c: PointOnObject(g2,g-3)
    c: Symmetric(g0,g0,g-2)
    c: PointOnObject(g2,g-4)
FEATURE [PartDesign::Pocket] Pocket004
  BaseFeature = -> Fillet001
  Direction = (0,0,-1)
  Length = 0
  Length2 = 5
  Profile = -> Sketch019
  ReferenceAxis = -> Sketch019 [N_Axis]
  Type = 3
  UpToFace = -> Fillet001 [Face23]
FEATURE [PartDesign::Pad] Pad016
  BaseFeature = -> Pocket004
  Direction = (0,-1,0)
  Length = 2
  Length2 = 10
  Profile = -> Pocket004 [Face10,Face26,Face39]
  Type = 0
FEATURE [PartDesign::Pad] Pad017
  BaseFeature = -> Pad016
  Direction = (0,1,0)
  Length = 2
  Length2 = 10
  Profile = -> Pad016 [Face13,Face34,Face50]
  Type = 0
FEATURE [App::Link] Baseplate  label="Baseplate001"
  AssemblyType = Part::Link
  AttachedBy = #LCS_0002
  AttachedTo = Parent Assembly#LCS_Origin
  LinkedObject = -> Part_2
  SolverId = Asm4EE
  expr: Placement = LCS_Origin.Placement * AttachmentOffset * LCS_0002.Placement ^ -1
FEATURE [PartDesign::Pocket] Pocket005
  BaseFeature = -> Pad017
  Direction = (0,0,-1)
  Length = 1
  Length2 = 5
  Profile = -> Pad017 [Face34,Face23,Face25,Face24]
  Type = 0
FEATURE [PartDesign::Pocket] Pocket006
  BaseFeature = -> Pad012
  Direction = (0,0,-1)
  Length = 1
  Length2 = 5
  Profile = -> Pad012 [Face8]
  Type = 0
FEATURE [Sketcher::SketchObject] Sketch020
  FullyConstrained = true
  MapMode = 5
  Placement = pos=(1,0,0) rot=(0.57735,0.57735,0.57735;2.0944rad)
  Support = -> [Pocket006]
  sketch-geometry (1):
    g0: Circle CenterX=0 CenterY=-0.3 CenterZ=0 NormalX=0 NormalY=0 NormalZ=1 AngleXU=0 Radius=0.65
  constraints (3):
    c: PointOnObject(g0,g-2)
    c: Radius(g0) = 0.65
    c: DistanceY(g0,g-1) = 0.3
FEATURE [PartDesign::Pocket] Pocket007
  BaseFeature = -> Pocket006
  Direction = (-1,0,0)
  Length = 5
  Length2 = 5
  Profile = -> Sketch020
  ReferenceAxis = -> Sketch020 [N_Axis]
  Type = 1
FEATURE [PartDesign::Body] Body_2
  Group = -> [Sketch013,Pad011,Sketch014,Pad012,Pocket006,Sketch020,Pocket007]
  Origin = -> Origin008
  Tip = -> Pocket007
FEATURE [PartDesign::CoordinateSystem] LCS_1
  AttacherType = Attacher::AttachEngine3D
  MapMode = 45
  Placement = pos=(0,0,-4) rot=(0,0.707107,0.707107;3.14159rad)
  Support = -> [Pocket007]
FEATURE [App::Part] Part_1  label="spring"
  Group = -> [LCS_0,Body_2,LCS_1]
  Origin = -> Origin007
FEATURE [PartDesign::CoordinateSystem] LCS_2
  AttacherType = Attacher::AttachEngine3D
  MapMode = 45
  Placement = pos=(3.31163,-2.85,-4) rot=(0,0.707107,0.707107;3.14159rad)
  Support = -> [Pocket005]
FEATURE [PartDesign::CoordinateSystem] LCS_3
  AttacherType = Attacher::AttachEngine3D
  MapMode = 45
  Placement = pos=(-2.22398,-5,-4) rot=(0,0.707107,0.707107;3.14159rad)
  Support = -> [Pocket005]
FEATURE [PartDesign::Pad] Pad018
  BaseFeature = -> Pocket005
  Direction = (1,0,0)
  Length = 1
  Length2 = 10
  Profile = -> Pocket005 [Face6]
  Type = 0
FEATURE [PartDesign::Pocket] Pocket008
  BaseFeature = -> Pad018
  Direction = (0,-1,0)
  Length = 0.1
  Length2 = 5
  Profile = -> Pad018 [Face21]
  Type = 0
FEATURE [PartDesign::Pocket] Pocket009
  BaseFeature = -> Pocket008
  Direction = (0,1,0)
  Length = 0.1
  Length2 = 5
  Profile = -> Pocket008 [Face22]
  Type = 0
FEATURE [PartDesign::Pocket] Pocket010
  BaseFeature = -> Pocket009
  Direction = (0,-1,0)
  Length = 0.1
  Length2 = 5
  Profile = -> Pocket009 [Face13]
  Type = 0
FEATURE [PartDesign::Pocket] Pocket011
  BaseFeature = -> Pocket010
  Direction = (0,1,0)
  Length = 0.1
  Length2 = 5
  Profile = -> Pocket010 [Face7]
  Type = 0
FEATURE [PartDesign::Body] Body002
  Group = -> [Sketch015,Pad013,Sketch016,Pad014,Sketch017,Pad015,Sketch018,Pocket003,Fillet001,Sketch019,Pocket004,Pad016,Pad017,Pocket005,Pad018,Pocket008,Pocket009,Pocket010,Pocket011]
  Origin = -> Origin010
  Tip = -> Pocket011
FEATURE [App::Part] Part_2  label="Baseplate"
  Group = -> [LCS_0002,Body002,LCS_2,LCS_3]
  Origin = -> Origin009
FEATURE [App::Link] spring  label="spring001"
  AssemblyType = Part::Link
  AttachedBy = #LCS_1
  AttachedTo = Baseplate#LCS_2
  AttachmentOffset = pos=(-0.3,0,0) rot=(0,0,1;0rad)
  LinkPlacement = pos=(3.61163,-2.85,0) rot=(0,0,1;0rad)
  LinkedObject = -> Part_1
  Placement = pos=(3.61163,-2.85,0) rot=(0,0,1;0rad)
  SolverId = Asm4EE
  expr: Placement = Baseplate.Placement * LCS_2.Placement * AttachmentOffset * LCS_1.Placement ^ -1
FEATURE [App::Link] spring001  label="spring002"
  AssemblyType = Part::Link
  AttachedBy = #LCS_1
  AttachedTo = Baseplate#LCS_3
  AttachmentOffset = pos=(0.3,0,0) rot=(0,1,0;3.14159rad)
  LinkPlacement = pos=(-2.52398,-5,0) rot=(0,0,1;3.14159rad)
  LinkedObject = -> Part_1
  Placement = pos=(-2.52398,-5,0) rot=(0,0,1;3.14159rad)
  SolverId = Asm4EE
  expr: Placement = Baseplate.Placement * LCS_3.Placement * AttachmentOffset * LCS_1.Placement ^ -1
FEATURE [App::Part] Model
  AssemblyType = Part::Link
  Group = -> [LCS_Origin,Constraints,Variables,Configurations,Baseplate,spring,spring001]
  Origin = -> Origin006
  Type = Assembly
FEATURE [PartDesign::CoordinateSystem] LCS_0003
  AttacherType = Attacher::AttachEngine3D
  MapMode = 2
  Support = -> [X_Axis011]
FEATURE [PartDesign::CoordinateSystem] LCS_0004
  AttacherType = Attacher::AttachEngine3D
  MapMode = 2
  Support = -> [X_Axis012]
FEATURE [Mesh::Feature] baseplate_left
FEATURE [Part::Feature] baseplate_left001
  shape: bbox 500 x 500 x 2.3 mm, 632 faces, 0 solids (baked)
FEATURE [Part::Refine] baseplate_left001001
  Source = -> baseplate_left001
FEATURE [Part::Feature] baseplate_left001001_solid  label="baseplate_left001001 (Solid)"
  shape: bbox 500 x 500 x 2.3 mm, 130 faces (baked)
FEATURE [PartDesign::FeatureBase] BaseFeature
  BaseFeature = -> baseplate_left001001_solid
FEATURE [Sketcher::SketchObject] Sketch021
  ExternalGeometry = -> [BaseFeature]
  FullyConstrained = true
  MapMode = 5
  Placement = pos=(0,0,0) rot=(0,1,0;3.14159rad)
  Support = -> [XY_Plane012]
  sketch-geometry (16):
    g0: LineSegment StartX=-211.098 StartY=171.423 StartZ=0 EndX=-187.375 EndY=147.7 EndZ=0
    g1: LineSegment StartX=-211.098 StartY=171.423 StartZ=0 EndX=-200.845 EndY=181.676 EndZ=0
    g2: LineSegment StartX=-200.845 StartY=181.676 StartZ=0 EndX=-190.592 EndY=171.423 EndZ=0
    g3: LineSegment StartX=-190.592 StartY=171.423 StartZ=0 EndX=-200.845 EndY=161.17 EndZ=0
    g4: LineSegment StartX=-200.845 StartY=161.17 StartZ=0 EndX=-211.098 EndY=171.423 EndZ=0
    g5: LineSegment StartX=-187.375 StartY=147.7 StartZ=0 EndX=-177.122 EndY=157.953 EndZ=0
    g6: LineSegment StartX=-177.122 StartY=157.953 StartZ=0 EndX=-187.375 EndY=168.206 EndZ=0
    g7: LineSegment StartX=-187.375 StartY=168.206 StartZ=0 EndX=-197.628 EndY=157.953 EndZ=0
    g8: LineSegment StartX=-197.628 StartY=157.953 StartZ=0 EndX=-187.375 EndY=147.7 EndZ=0
    g9: LineSegment StartX=-180.64 StartY=167.906 StartZ=0 EndX=-170.387 EndY=178.159 EndZ=0
    g10: LineSegment StartX=-170.387 StartY=178.159 StartZ=0 EndX=-180.64 EndY=188.412 EndZ=0
    g11: LineSegment StartX=-180.64 StartY=188.412 StartZ=0 EndX=-190.893 EndY=178.159 EndZ=0
    g12: LineSegment StartX=-190.893 StartY=178.159 StartZ=0 EndX=-180.64 EndY=167.906 EndZ=0
    g13: LineSegment StartX=-190.592 StartY=171.423 StartZ=0 EndX=-187.375 EndY=174.641 EndZ=0
    g14: LineSegment StartX=-200.845 StartY=181.676 StartZ=0 EndX=-190.893 EndY=178.159 EndZ=0
    g15: LineSegment StartX=-180.64 StartY=167.906 StartZ=0 EndX=-177.122 EndY=157.953 EndZ=0
  constraints (45):
    c: Coincident(g1,g2)
    c: Coincident(g2,g3)
    c: Coincident(g3,g4)
    c: Coincident(g4,g1)
    c: PointOnObject(g3,g0)
    c: Equal(g4,g3)
    c: Equal(g3,g1)
    c: Equal(g1,g2)
    c: Perpendicular(g4,g1)
    c: Distance(g1) = 14.5
    c: Coincident(g0,g1)
    c: Coincident(g0,g5)
    c: Coincident(g5,g6)
    c: Coincident(g6,g7)
    c: PointOnObject(g7,g0)
    c: Coincident(g7,g8)
    c: Coincident(g8,g5)
    c: Equal(g7,g8)
    c: Equal(g8,g6)
    c: Equal(g6,g5)
    c: Equal(g5,g4)
    c: Perpendicular(g8,g7)
    c: Distance(g1,g7) = 19.05
    c: Coincident(g9,g10)
    c: Coincident(g10,g11)
    c: Coincident(g11,g12)
    c: Coincident(g12,g9)
    c: Equal(g11,g12)
    c: Equal(g12,g10)
    c: Equal(g10,g9)
    c: Perpendicular(g12,g11)
    c: Parallel(g2,g12)
    c: Coincident(g13,g2)
    c: PointOnObject(g13,g12)
    c: Perpendicular(g12,g13)
    c: Distance(g13,g3) = 19.05
    c: Coincident(g14,g1)
    c: Coincident(g14,g11)
    c: Coincident(g15,g9)
    c: Coincident(g15,g5)
    c: Equal(g15,g14)
    c: Equal(g6,g10)
    c: Angle(g8,g-1) = 0.785398
    c: DistanceX(g-3,g5) = 20
    c: DistanceY(g-3,g5) = 7
FEATURE [PartDesign::Pocket] Pocket012
  BaseFeature = -> BaseFeature
  Direction = (0,0,1)
  Length = 5
  Length2 = 5
  Profile = -> Sketch021
  ReferenceAxis = -> Sketch021 [N_Axis]
  Type = 0
FEATURE [Sketcher::SketchObject] Sketch022
  ExternalGeometry = -> [Pocket012]
  FullyConstrained = false
  MapMode = 5
  Placement = pos=(0,0,2.3) rot=(0,0,1;0rad)
  Support = -> [Pocket012]
  sketch-geometry (22):
    g0: LineSegment StartX=160.64 StartY=198.412 StartZ=0 EndX=200.64 EndY=198.412 EndZ=0
    g1: LineSegment StartX=49.525 StartY=40 StartZ=0 EndX=263.025 EndY=40 EndZ=0
    g2: LineSegment StartX=227.375 StartY=106.5 StartZ=0 EndX=230.175 EndY=106.5 EndZ=0
    g3: LineSegment StartX=230.175 StartY=106.5 StartZ=0 EndX=230.175 EndY=50 EndZ=0
    g4: LineSegment StartX=230.175 StartY=50 StartZ=0 EndX=227.375 EndY=50 EndZ=0
    g5: LineSegment StartX=227.375 StartY=50 StartZ=0 EndX=227.375 EndY=106.5 EndZ=0
    g6: LineSegment StartX=253.025 StartY=106.5 StartZ=0 EndX=250.225 EndY=106.5 EndZ=0
    g7: LineSegment StartX=250.225 StartY=106.5 StartZ=0 EndX=250.225 EndY=50 EndZ=0
    g8: LineSegment StartX=250.225 StartY=50 StartZ=0 EndX=253.025 EndY=50 EndZ=0
    g9: LineSegment StartX=253.025 StartY=50 StartZ=0 EndX=253.025 EndY=106.5 EndZ=0
    g10: LineSegment StartX=227.375 StartY=106.5 StartZ=0 EndX=228.775 EndY=106.5 EndZ=0
    g11: LineSegment StartX=228.775 StartY=106.5 StartZ=0 EndX=230.175 EndY=106.5 EndZ=0
    g12: LineSegment StartX=253.025 StartY=106.5 StartZ=0 EndX=251.625 EndY=106.5 EndZ=0
    g13: LineSegment StartX=251.625 StartY=106.5 StartZ=0 EndX=250.225 EndY=106.5 EndZ=0
    g14: LineSegment StartX=200.64 StartY=198.412 StartZ=0 EndX=263.025 EndY=163.412 EndZ=0
    g15: LineSegment StartX=263.025 StartY=163.412 StartZ=0 EndX=263.025 EndY=40 EndZ=0
    g16: LineSegment StartX=49.525 StartY=40 StartZ=0 EndX=49.525 EndY=163.412 EndZ=0
    g17: LineSegment StartX=49.525 StartY=163.412 StartZ=0 EndX=160.64 EndY=198.412 EndZ=0
    g18: LineSegment StartX=0 StartY=0 StartZ=0 EndX=511.801 EndY=0 EndZ=0
    g19: LineSegment StartX=511.801 StartY=0 StartZ=0 EndX=511.801 EndY=507.959 EndZ=0
    g20: LineSegment StartX=511.801 StartY=507.959 StartZ=0 EndX=0 EndY=507.959 EndZ=0
    g21: LineSegment StartX=0 StartY=507.959 StartZ=0 EndX=0 EndY=0 EndZ=0
  constraints (61):
    c: Coincident(g0,g14)
    c: Coincident(g17,g0)
    c: Coincident(g1,g15)
    c: Coincident(g2,g3)
    c: Coincident(g3,g4)
    c: Coincident(g4,g5)
    c: Coincident(g5,g2)
    c: Horizontal(g2)
    c: Horizontal(g4)
    c: Vertical(g3)
    c: Vertical(g5)
    c: Coincident(g6,g7)
    c: Coincident(g7,g8)
    c: Coincident(g8,g9)
    c: Coincident(g9,g6)
    c: Horizontal(g6)
    c: Horizontal(g8)
    c: Vertical(g7)
    c: Vertical(g9)
    c: Coincident(g10,g2)
    c: Coincident(g11,g10)
    c: Coincident(g11,g2)
    c: Equal(g11,g10)
    c: PointOnObject(g10,g2)
    c: Coincident(g6,g12)
    c: Coincident(g12,g13)
    c: Coincident(g13,g6)
    c: Equal(g13,g12)
    c: PointOnObject(g12,g6)
    c: DistanceX(g10,g12) = 22.85
    c: Equal(g2,g6)
    c: DistanceX(g4,g4) = 2.8
    c: DistanceY(g5,g5) = 56.5
    c: PointOnObject(g6,g2)
    c: PointOnObject(g8,g4)
    c: Horizontal(g1)
    c: DistanceX(g-3,g2) = 20
    c: DistanceY(g4,g-4) = 0
    c: DistanceY(g15,g-4) = 10
    c: DistanceX(g16,g-6) = 10
    c: DistanceX(g8,g15) = 10
    c: Coincident(g14,g15)
    c: Vertical(g15)
    c: Horizontal(g0)
    c: DistanceY(g-5,g0) = 10
    c: Coincident(g16,g17)
    c: Vertical(g16)
    c: DistanceY(g16,g-5) = 25
    c: DistanceY(g14,g-5) = 25
    c: DistanceX(g0,g-5) = 20
    c: DistanceX(g-5,g0) = 20
    c: Coincident(g1,g16)
    c: Coincident(g18,g19)
    c: Coincident(g19,g20)
    c: Coincident(g20,g21)
    c: Coincident(g21,g18)
    c: Horizontal(g18)
    c: Horizontal(g20)
    c: Vertical(g19)
    c: Vertical(g21)
    c: Coincident(g18,g-1)
FEATURE [PartDesign::Pocket] Pocket013
  BaseFeature = -> Pocket012
  Direction = (0,0,-1)
  Length = 5
  Length2 = 5
  Profile = -> Sketch022
  ReferenceAxis = -> Sketch022 [N_Axis]
  Type = 0
FEATURE [PartDesign::CoordinateSystem] LCS_0005
  AttacherType = Attacher::AttachEngine3D
  MapMode = 2
  Support = -> [X_Axis]
FEATURE [Mesh::Feature] baseplate_right
FEATURE [Part::Feature] baseplate_right001
  shape: bbox 500 x 500 x 2.3 mm, 652 faces, 0 solids (baked)
FEATURE [Part::Refine] baseplate_right001001
  Source = -> baseplate_right001
FEATURE [Part::Feature] baseplate_right001001_solid  label="baseplate_right001001 (Solid)"
  shape: bbox 500 x 500 x 2.3 mm, 134 faces (baked)
FEATURE [PartDesign::FeatureBase] BaseFeature001
  BaseFeature = -> baseplate_right001001_solid
FEATURE [Sketcher::SketchObject] Sketch024
  ExternalGeometry = -> [BaseFeature001]
  FullyConstrained = true
  MapMode = 5
  Placement = pos=(0,0,0) rot=(1,0,0;3.14159rad)
  Support = -> [BaseFeature001]
  expr: Constraints[40] = 1.25 * 19.05
  sketch-geometry (16):
    g0: LineSegment StartX=42.6282 StartY=-166.401 StartZ=0 EndX=64.1937 EndY=-140.7 EndZ=0
    g1: LineSegment StartX=42.6282 StartY=-166.401 StartZ=0 EndX=31.5206 EndY=-157.08 EndZ=0
    g2: LineSegment StartX=31.5206 StartY=-157.08 StartZ=0 EndX=40.841 EndY=-145.973 EndZ=0
    g3: LineSegment StartX=40.841 StartY=-145.973 StartZ=0 EndX=51.9486 EndY=-155.293 EndZ=0
    g4: LineSegment StartX=51.9486 StartY=-155.293 StartZ=0 EndX=42.6282 EndY=-166.401 EndZ=0
    g5: LineSegment StartX=54.8733 StartY=-151.808 StartZ=0 EndX=43.7657 EndY=-142.487 EndZ=0
    g6: LineSegment StartX=43.7657 StartY=-142.487 StartZ=0 EndX=53.0861 EndY=-131.38 EndZ=0
    g7: LineSegment StartX=53.0861 StartY=-131.38 StartZ=0 EndX=64.1937 EndY=-140.7 EndZ=0
    g8: LineSegment StartX=64.1937 StartY=-140.7 StartZ=0 EndX=54.8733 EndY=-151.808 EndZ=0
    g9: LineSegment StartX=42.6282 StartY=-166.401 StartZ=0 EndX=53.411 EndY=-153.55 EndZ=0
    g10: LineSegment StartX=53.411 StartY=-153.55 StartZ=0 EndX=64.1937 EndY=-140.7 EndZ=0
    g11: LineSegment StartX=53.411 StartY=-153.55 StartZ=0 EndX=71.6524 EndY=-168.857 EndZ=0
    g12: LineSegment StartX=65.205 StartY=-153.983 StartZ=0 EndX=76.3126 EndY=-163.303 EndZ=0
    g13: LineSegment StartX=76.3126 StartY=-163.303 StartZ=0 EndX=66.9922 EndY=-174.411 EndZ=0
    g14: LineSegment StartX=66.9922 StartY=-174.411 StartZ=0 EndX=55.8846 EndY=-165.09 EndZ=0
    g15: LineSegment StartX=55.8846 StartY=-165.09 StartZ=0 EndX=65.205 EndY=-153.983 EndZ=0
  constraints (44):
    c: Coincident(g0,g1)
    c: Coincident(g1,g2)
    c: Coincident(g2,g3)
    c: PointOnObject(g3,g0)
    c: Coincident(g3,g4)
    c: Coincident(g4,g1)
    c: PointOnObject(g5,g0)
    c: Coincident(g5,g6)
    c: Coincident(g6,g7)
    c: Coincident(g7,g0)
    c: Coincident(g7,g8)
    c: Coincident(g8,g5)
    c: Equal(g1,g2)
    c: Equal(g2,g3)
    c: Equal(g3,g4)
    c: Equal(g4,g5)
    c: Equal(g5,g6)
    c: Equal(g6,g7)
    c: Equal(g7,g8)
    c: Perpendicular(g8,g5)
    c: Perpendicular(g4,g1)
    c: Distance(g1,g5) = 19.05
    c: Distance(g2) = 14.5
    c: Coincident(g9,g1)
    c: Coincident(g10,g9)
    c: Coincident(g10,g7)
    c: Equal(g9,g10)
    c: PointOnObject(g9,g0)
    c: Coincident(g11,g9)
    c: Perpendicular(g0,g11)
    c: Coincident(g12,g13)
    c: Coincident(g13,g14)
    c: Coincident(g14,g15)
    c: Coincident(g15,g12)
    c: Symmetric(g12,g14,g11)
    c: Symmetric(g12,g13,g11)
    c: Equal(g12,g15)
    c: Equal(g14,g13)
    c: Equal(g13,g8)
    c: PointOnObject(g11,g13)
    c: Distance(g11,g9) = 23.8125
    c: Angle(g7,g-3) = 0.698132
    c: DistanceX(g7,g-3) = 12
    c: PointOnObject(g7,g-3)
FEATURE [PartDesign::Pocket] Pocket014
  BaseFeature = -> BaseFeature001
  Direction = (0,0,1)
  Length = 5
  Length2 = 5
  Profile = -> Sketch024
  ReferenceAxis = -> Sketch024 [N_Axis]
  Type = 0
FEATURE [Sketcher::SketchObject] Sketch025
  ExternalGeometry = -> [Pocket014]
  FullyConstrained = true
  MapMode = 5
  Placement = pos=(0,0,0) rot=(1,0,0;3.14159rad)
  Support = -> [Pocket014]
  sketch-geometry (24):
    g0: LineSegment StartX=0.875002 StartY=-43 StartZ=0 EndX=214.375 EndY=-43 EndZ=0
    g1: LineSegment StartX=214.375 StartY=-43 StartZ=0 EndX=214.375 EndY=-143.007 EndZ=0
    g2: LineSegment StartX=214.375 StartY=-143.007 StartZ=0 EndX=66.9922 EndY=-181.411 EndZ=0
    g3: LineSegment StartX=66.9922 StartY=-181.411 StartZ=0 EndX=0.875002 EndY=-160.593 EndZ=0
    g4: LineSegment StartX=0.875002 StartY=-160.593 StartZ=0 EndX=0.875002 EndY=-43 EndZ=0
    g5: LineSegment StartX=42.6282 StartY=-166.401 StartZ=0 EndX=40.526 EndY=-173.078 EndZ=0
    g6: LineSegment StartX=66.9922 StartY=-181.411 StartZ=0 EndX=66.9922 EndY=-174.411 EndZ=0
    g7: LineSegment StartX=195.469 StartY=-140.7 StartZ=0 EndX=197.234 EndY=-147.474 EndZ=0
    g8: LineSegment StartX=8.875 StartY=-50 StartZ=0 EndX=11.675 EndY=-50 EndZ=0
    g9: LineSegment StartX=11.675 StartY=-50 StartZ=0 EndX=11.675 EndY=-106.5 EndZ=0
    g10: LineSegment StartX=11.675 StartY=-106.5 StartZ=0 EndX=8.875 EndY=-106.5 EndZ=0
    g11: LineSegment StartX=8.875 StartY=-106.5 StartZ=0 EndX=8.875 EndY=-50 EndZ=0
    g12: LineSegment StartX=31.725 StartY=-50 StartZ=0 EndX=34.525 EndY=-50 EndZ=0
    g13: LineSegment StartX=34.525 StartY=-50 StartZ=0 EndX=34.525 EndY=-106.5 EndZ=0
    g14: LineSegment StartX=34.525 StartY=-106.5 StartZ=0 EndX=31.725 EndY=-106.5 EndZ=0
    g15: LineSegment StartX=31.725 StartY=-106.5 StartZ=0 EndX=31.725 EndY=-50 EndZ=0
    g16: LineSegment StartX=8.875 StartY=-50 StartZ=0 EndX=10.275 EndY=-50 EndZ=0
    g17: LineSegment StartX=10.275 StartY=-50 StartZ=0 EndX=11.675 EndY=-50 EndZ=0
    g18: LineSegment StartX=31.725 StartY=-50 StartZ=0 EndX=33.125 EndY=-50 EndZ=0
    g19: LineSegment StartX=33.125 StartY=-50 StartZ=0 EndX=34.525 EndY=-50 EndZ=0
    g20: LineSegment StartX=0 StartY=0 StartZ=0 EndX=798.95 EndY=0 EndZ=0
    g21: LineSegment StartX=798.95 StartY=0 StartZ=0 EndX=798.95 EndY=-762.419 EndZ=0
    g22: LineSegment StartX=798.95 StartY=-762.419 StartZ=0 EndX=0 EndY=-762.419 EndZ=0
    g23: LineSegment StartX=0 StartY=-762.419 StartZ=0 EndX=0 EndY=0 EndZ=0
  constraints (68):
    c: Horizontal(g0)
    c: Coincident(g0,g1)
    c: Vertical(g1)
    c: Coincident(g1,g2)
    c: Coincident(g2,g3)
    c: Coincident(g3,g4)
    c: Coincident(g4,g0)
    c: Vertical(g4)
    c: DistanceX(g-3,g1) = 7
    c: Coincident(g5,g-4)
    c: PointOnObject(g5,g3)
    c: Perpendicular(g3,g5)
    c: Distance(g5) = 7
    c: Coincident(g6,g2)
    c: Coincident(g6,g-5)
    c: Vertical(g6)
    c: DistanceY(g6,g6) = 7
    c: Coincident(g7,g-6)
    c: PointOnObject(g7,g2)
    c: Perpendicular(g2,g7)
    c: Distance(g7) = 7
    c: DistanceY(g-7,g0) = 7
    c: Coincident(g8,g9)
    c: Coincident(g9,g10)
    c: Coincident(g10,g11)
    c: Coincident(g11,g8)
    c: Horizontal(g8)
    c: Horizontal(g10)
    c: Vertical(g9)
    c: Vertical(g11)
    c: Coincident(g12,g13)
    c: Coincident(g13,g14)
    c: Coincident(g14,g15)
    c: Coincident(g15,g12)
    c: Horizontal(g12)
    c: Horizontal(g14)
    c: Vertical(g13)
    c: Vertical(g15)
    c: Coincident(g16,g8)
    c: Coincident(g17,g16)
    c: Coincident(g17,g8)
    c: Equal(g17,g16)
    c: Horizontal(g16)
    c: Coincident(g12,g18)
    c: Coincident(g18,g19)
    c: Coincident(g19,g12)
    c: Equal(g19,g18)
    c: Horizontal(g19)
    c: PointOnObject(g8,g12)
    c: Equal(g11,g15)
    c: Equal(g10,g14)
    c: DistanceX(g16,g18) = 22.85
    c: DistanceY(g11,g11) = 56.5
    c: DistanceX(g10,g10) = 2.8
    c: DistanceY(g8,g0) = 7
    c: DistanceX(g0,g8) = 8
    c: Coincident(g20,g21)
    c: Coincident(g21,g22)
    c: Coincident(g22,g23)
    c: Coincident(g23,g20)
    c: Horizontal(g20)
    c: Horizontal(g22)
    c: Vertical(g21)
    c: Vertical(g23)
    c: Coincident(g20,g-1)
    c: DistanceX(g21) = 798.95
    c: DistanceY(g21) = -762.419
    c: DistanceX(g12,g-8) = 25
FEATURE [PartDesign::Pocket] Pocket015
  BaseFeature = -> Pocket014
  Direction = (0,0,1)
  Length = 5
  Length2 = 5
  Profile = -> Sketch025
  ReferenceAxis = -> Sketch025 [N_Axis]
  Type = 0
FEATURE [Sketcher::SketchObject] Sketch026
  ExternalGeometry = -> [Pocket015]
  FullyConstrained = true
  MapMode = 5
  Placement = pos=(0,0,2.3) rot=(0,0,1;0rad)
  Support = -> [Pocket015]
  sketch-geometry (10):
    g0: LineSegment StartX=0.875002 StartY=160.593 StartZ=0 EndX=66.9922 EndY=181.411 EndZ=0
    g1: LineSegment StartX=66.9922 StartY=181.411 StartZ=0 EndX=214.375 EndY=143.007 EndZ=0
    g2: LineSegment StartX=214.375 StartY=143.007 StartZ=0 EndX=214.375 EndY=43 EndZ=0
    g3: LineSegment StartX=214.375 StartY=43 StartZ=0 EndX=0.875002 EndY=43 EndZ=0
    g4: LineSegment StartX=0.875002 StartY=43 StartZ=0 EndX=0.875002 EndY=160.593 EndZ=0
    g5: LineSegment StartX=212.375 StartY=141.462 StartZ=0 EndX=212.375 EndY=45 EndZ=0
    g6: LineSegment StartX=212.375 StartY=45 StartZ=0 EndX=2.875 EndY=45 EndZ=0
    g7: LineSegment StartX=2.875 StartY=45 StartZ=0 EndX=2.875 EndY=159.126 EndZ=0
    g8: LineSegment StartX=2.875 StartY=159.126 StartZ=0 EndX=67.0444 EndY=179.33 EndZ=0
    g9: LineSegment StartX=67.0444 StartY=179.33 StartZ=0 EndX=212.375 EndY=141.462 EndZ=0
  constraints (21):
    c: Coincident(g-7,g0)
    c: Coincident(g0,g-4)
    c: Coincident(g0,g1)
    c: Coincident(g1,g-5)
    c: Coincident(g1,g2)
    c: Coincident(g2,g-6)
    c: Coincident(g2,g3)
    c: Coincident(g3,g-7)
    c: Coincident(g3,g4)
    c: Coincident(g4,g0)
    c: Coincident(g5,g6)
    c: Coincident(g5,g9)
    c: Coincident(g6,g7)
    c: Coincident(g7,g8)
    c: Coincident(g8,g9)
    c: Block(g9)
    c: Block(g5)
    c: Parallel(g0,g8)
    c: DistanceX(g3,g6) = 2
    c: Vertical(g7)
    c: Horizontal(g6)
FEATURE [PartDesign::Pad] Pad020
  BaseFeature = -> Pocket015
  Direction = (0,0,1)
  Length = 15
  Length2 = 10
  Profile = -> Sketch026
  ReferenceAxis = -> Sketch026 [N_Axis]
  Type = 0
FEATURE [Sketcher::SketchObject] Sketch027
  ExternalGeometry = -> [Pad020]
  FullyConstrained = true
  MapMode = 5
  Placement = pos=(0,0,2.3) rot=(0,0,1;0rad)
  Support = -> [Pad020]
  sketch-geometry (10):
    g0: LineSegment StartX=88.1 StartY=64.5 StartZ=0 EndX=88.1 EndY=66.775 EndZ=0
    g1: LineSegment StartX=88.1 StartY=66.775 StartZ=0 EndX=88.1 EndY=69.05 EndZ=0
    g2: LineSegment StartX=88.1 StartY=66.775 StartZ=0 EndX=212.375 EndY=66.775 EndZ=0
    g3: LineSegment StartX=56.525 StartY=66 StartZ=0 EndX=56.525 EndY=67.55 EndZ=0
    g4: LineSegment StartX=56.525 StartY=67.55 StartZ=0 EndX=212.375 EndY=67.55 EndZ=0
    g5: LineSegment StartX=212.375 StartY=67.55 StartZ=0 EndX=212.375 EndY=66 EndZ=0
    g6: LineSegment StartX=212.375 StartY=66 StartZ=0 EndX=56.525 EndY=66 EndZ=0
    g7: GeomPoint X=134.45 Y=66.775 Z=0
    g8: LineSegment StartX=97.625 StartY=83.55 StartZ=0 EndX=97.625 EndY=85.825 EndZ=0
    g9: LineSegment StartX=97.625 StartY=85.825 StartZ=0 EndX=97.625 EndY=88.1 EndZ=0
  constraints (29):
    c: Coincident(g-4,g0)
    c: Vertical(g0)
    c: Coincident(g0,g1)
    c: Vertical(g1)
    c: Equal(g1,g0)
    c: Coincident(g2,g0)
    c: PointOnObject(g2,g-3)
    c: Horizontal(g2)
    c: Coincident(g3,g4)
    c: Coincident(g4,g5)
    c: Coincident(g5,g6)
    c: Coincident(g6,g3)
    c: Vertical(g3)
    c: Vertical(g5)
    c: Horizontal(g4)
    c: Horizontal(g6)
    c: Symmetric(g5,g3,g7)
    c: PointOnObject(g7,g2)
    c: PointOnObject(g5,g-3)
    c: PointOnObject(g1,g-5)
    c: DistanceY(g0,g3) = 1.5
    c: DistanceX(g-6,g3) = 22
    c: Coincident(g8,g-7)
    c: Vertical(g8)
    c: Coincident(g9,g8)
    c: PointOnObject(g9,g-8)
    c: Vertical(g9)
    c: Equal(g9,g8)
    c: DistanceY(g0,g8) = 19.05  'wall_row_distance'
FEATURE [PartDesign::Pad] Pad021
  BaseFeature = -> Pad020
  Direction = (0,0,1)
  Length = 20
  Length2 = 10
  Profile = -> Sketch027
  ReferenceAxis = -> Sketch027 [N_Axis]
  Type = 3
  UpToFace = -> Pad020 [Face161]
FEATURE [PartDesign::LinearPattern] LinearPattern
  BaseFeature = -> Pad021
  Direction = -> Sketch027 [V_Axis]
  Length = 57.15
  Mode = 0
  Occurrences = 4
  Offset = 19.05
  Originals = -> [Pad021]
  expr: Length = Sketch027.Constraints.wall_row_distance * (Occurrences - 1)
FEATURE [PartDesign::Pad] Pad022
  BaseFeature = -> LinearPattern
  Direction = (-1,0,0)
  Length = 10
  Length2 = 10
  Profile = -> LinearPattern [Face164]
  Type = 2
FEATURE [PartDesign::Pad] Pad023
  BaseFeature = -> Pad022
  Direction = (-1,0,0)
  Length = 2
  Length2 = 10
  Profile = -> Pad022 [Face170]
  Type = 0
FEATURE [PartDesign::Pad] Pad024
  BaseFeature = -> Pad023
  Direction = (0,-1,0)
  Length = 10
  Length2 = 10
  Profile = -> Pad023 [Face171]
  Type = 2
FEATURE [PartDesign::Pad] Pad025
  BaseFeature = -> Pad024
  Direction = (0,1,0)
  Length = 10
  Length2 = 10
  Profile = -> Pad024 [Face179]
  Type = 2
FEATURE [PartDesign::Pocket] Pocket016
  BaseFeature = -> Pad025
  Direction = (0,0,-1)
  Length = 8
  Length2 = 5
  Profile = -> Pad025 [Face201,Face202,Face199]
  Type = 0
FEATURE [PartDesign::Pocket] Pocket017
  BaseFeature = -> Pocket016
  Direction = (0,0,-1)
  Length = 8
  Length2 = 5
  Profile = -> Pocket016 [Face200]
  Type = 0
FEATURE [PartDesign::Pad] Pad026
  BaseFeature = -> Pocket013
  Direction = (1,0,0)
  Length = 10
  Length2 = 10
  Profile = -> Pocket013 [Face117]
  Type = 2
FEATURE [PartDesign::Body] Body_3  label="plate_left"
  BaseFeature = -> baseplate_left001001_solid
  Group = -> [BaseFeature,LCS_0004,Sketch021,Pocket012,Sketch022,Pocket013,Pad026]
  Origin = -> Origin012
  Tip = -> Pocket013
FEATURE [PartDesign::Pocket] Pocket018
  BaseFeature = -> Pocket017
  Direction = (0,0,1)
  Length = 0.9
  Length2 = 5
  Profile = -> Pocket017 [Face1]
  Type = 0
FEATURE [Sketcher::SketchObject] Sketch028
  FullyConstrained = false
  MapMode = 5
  Placement = pos=(0,0,0.9) rot=(1,0,0;3.14159rad)
  Support = -> [Pocket018]
  sketch-geometry (8):
    g0: LineSegment StartX=186.641 StartY=-48.1554 StartZ=0 EndX=186.641 EndY=-65.87 EndZ=0
    g1: LineSegment StartX=186.641 StartY=-65.87 StartZ=0 EndX=203.656 EndY=-65.87 EndZ=0
    g2: LineSegment StartX=203.656 StartY=-65.87 StartZ=0 EndX=203.656 EndY=-48.1554 EndZ=0
    g3: LineSegment StartX=203.656 StartY=-48.1554 StartZ=0 EndX=186.641 EndY=-48.1554 EndZ=0
    g4: LineSegment StartX=-16.894 StartY=-28.9206 StartZ=0 EndX=-16.894 EndY=-187.952 EndZ=0
    g5: LineSegment StartX=-16.894 StartY=-187.952 StartZ=0 EndX=239.258 EndY=-187.952 EndZ=0
    g6: LineSegment StartX=239.258 StartY=-187.952 StartZ=0 EndX=239.258 EndY=-28.9206 EndZ=0
    g7: LineSegment StartX=239.258 StartY=-28.9206 StartZ=0 EndX=-16.894 EndY=-28.9206 EndZ=0
  constraints (16):
    c: Coincident(g0,g1)
    c: Coincident(g1,g2)
    c: Coincident(g2,g3)
    c: Coincident(g3,g0)
    c: Vertical(g0)
    c: Vertical(g2)
    c: Horizontal(g1)
    c: Horizontal(g3)
    c: Coincident(g4,g5)
    c: Coincident(g5,g6)
    c: Coincident(g6,g7)
    c: Coincident(g7,g4)
    c: Vertical(g4)
    c: Vertical(g6)
    c: Horizontal(g5)
    c: Horizontal(g7)
FEATURE [PartDesign::Pocket] Pocket019
  BaseFeature = -> Pocket018
  Direction = (0,0,1)
  Length = 5
  Length2 = 5
  Profile = -> Sketch028
  ReferenceAxis = -> Sketch028 [N_Axis]
  Type = 1
FEATURE [Spreadsheet::Sheet] Spreadsheet
  cells = A1(horizontal_pad)=0.4; B1='switch_hole_size; C1='d_key; D1='h_plate; E1='h_wall_out; F1='d_wall_out; G1='h_wall_in; B2(switch_hole_size)=14.1; C2(d_key)=19.05; D2(h_plate)=1.5; E2(h_wall_out)=15; F2(d_wall_out)=2; G2(h_wall_in)=8
FEATURE [PartDesign::Pad] Pad027
  BaseFeature = -> Pocket019
  Direction = (-1,0,0)
  Length = 0.4
  Length2 = 10
  Profile = -> Pocket019 [Face8]
  Type = 0
  expr: Length = Spreadsheet.horizontal_pad
FEATURE [PartDesign::Pad] Pad028
  BaseFeature = -> Pad027
  Direction = (0,-1,0)
  Length = 0.4
  Length2 = 10
  Profile = -> Pad027 [Face6]
  Type = 0
  expr: Length = Spreadsheet.horizontal_pad
FEATURE [PartDesign::Body] plate_right
  BaseFeature = -> baseplate_right001001_solid
  Group = -> [BaseFeature001,LCS_0005,Sketch024,Pocket014,Sketch025,Pocket015,Sketch026,Pad020,Sketch027,Pad021,LinearPattern,Pad022,Pad023,Pad024,Pad025,Pocket016,Pocket017,Pocket018,Sketch028,Pocket019,Pad027,Pad028]
  Origin = -> Origin
  Tip = -> Pocket018
FEATURE [Mesh::Feature] baseplate_right_v2
FEATURE [Part::Feature] baseplate_right_v003
  shape: bbox 500 x 500 x 1.5 mm, 652 faces, 0 solids (baked)
FEATURE [Part::Refine] baseplate_right_v004
  Source = -> baseplate_right_v003
FEATURE [Part::Feature] baseplate_right_v004_solid001  label="baseplate_right_v004 (Solid)"
  shape: bbox 500 x 500 x 1.5 mm, 134 faces (baked)
FEATURE [PartDesign::FeatureBase] BaseFeature002
  BaseFeature = -> baseplate_right_v004_solid001
FEATURE [Sketcher::SketchObject] Sketch029
  AttachmentOffset = pos=(0,0,10) rot=(0,0,1;0rad)
  ExternalGeometry = -> [BaseFeature002]
  FullyConstrained = true
  MapMode = 5
  Placement = pos=(0,0,10) rot=(0,0,1;0rad)
  Support = -> [XY_Plane013]
  expr: Constraints[24] = Spreadsheet.d_key
  expr: Constraints[9] = Spreadsheet.switch_hole_size
  sketch-geometry (19):
    g0: LineSegment StartX=155.753 StartY=278.77 StartZ=0 EndX=145.783 EndY=268.8 EndZ=0
    g1: LineSegment StartX=145.783 StartY=268.8 StartZ=0 EndX=155.753 EndY=258.83 EndZ=0
    g2: LineSegment StartX=155.753 StartY=258.83 StartZ=0 EndX=165.723 EndY=268.8 EndZ=0
    g3: LineSegment StartX=165.723 StartY=268.8 StartZ=0 EndX=155.753 EndY=278.77 EndZ=0
    g4: GeomPoint X=155.753 Y=268.8 Z=0
    g5: LineSegment StartX=169.224 StartY=265.3 StartZ=0 EndX=159.253 EndY=255.33 EndZ=0
    g6: LineSegment StartX=159.253 StartY=255.33 StartZ=0 EndX=169.224 EndY=245.359 EndZ=0
    g7: LineSegment StartX=169.224 StartY=245.359 StartZ=0 EndX=179.194 EndY=255.33 EndZ=0
    g8: LineSegment StartX=179.194 StartY=255.33 StartZ=0 EndX=169.224 EndY=265.3 EndZ=0
    g9: GeomPoint X=169.224 Y=255.33 Z=0
    g10: LineSegment StartX=155.753 StartY=268.8 StartZ=0 EndX=169.224 EndY=255.33 EndZ=0
    g11: LineSegment StartX=180.166 StartY=289.713 StartZ=0 EndX=170.196 EndY=279.742 EndZ=0
    g12: LineSegment StartX=170.196 StartY=279.742 StartZ=0 EndX=180.166 EndY=269.772 EndZ=0
    g13: LineSegment StartX=180.166 StartY=269.772 StartZ=0 EndX=190.136 EndY=279.742 EndZ=0
    g14: LineSegment StartX=190.136 StartY=279.742 StartZ=0 EndX=180.166 EndY=289.713 EndZ=0
    g15: GeomPoint X=180.166 Y=279.742 Z=0
    g16: LineSegment StartX=162.488 StartY=262.065 StartZ=0 EndX=180.166 EndY=279.742 EndZ=0
    g17: LineSegment StartX=179.194 StartY=255.33 StartZ=0 EndX=180.166 EndY=269.772 EndZ=0
    g18: LineSegment StartX=170.196 StartY=279.742 StartZ=0 EndX=155.753 EndY=278.77 EndZ=0
  constraints (49):
    c: Coincident(g0,g1)
    c: Coincident(g1,g2)
    c: Coincident(g2,g3)
    c: Coincident(g3,g0)
    c: Symmetric(g2,g0,g4)
    c: Equal(g0,g1)
    c: Parallel(g1,g3)
    c: Parallel(g2,g0)
    c: Perpendicular(g1,g0)
    c: Distance(g1) = 14.1
    c: Coincident(g5,g6)
    c: Coincident(g6,g7)
    c: Coincident(g7,g8)
    c: Coincident(g8,g5)
    c: Symmetric(g7,g5,g9)
    c: Equal(g5,g6)
    c: Parallel(g5,g7)
    c: Parallel(g6,g8)
    c: Perpendicular(g5,g6)
    c: Parallel(g6,g1)
    c: Coincident(g10,g4)
    c: Coincident(g10,g9)
    c: Perpendicular(g2,g10)
    c: Equal(g1,g6)
    c: Distance(g10) = 19.05
    c: Coincident(g11,g12)
    c: Coincident(g12,g13)
    c: Coincident(g13,g14)
    c: Coincident(g14,g11)
    c: Symmetric(g13,g11,g15)
    c: Parallel(g13,g11)
    c: Parallel(g12,g14)
    c: Perpendicular(g12,g11)
    c: Equal(g12,g3)
    c: Equal(g12,g11)
    c: PointOnObject(g16,g10)
    c: Coincident(g16,g15)
    c: Perpendicular(g10,g16)
    c: Perpendicular(g12,g16)
    c: Angle(g10,g-1) = 0.785398
    c: Coincident(g17,g7)
    c: Coincident(g17,g12)
    c: Coincident(g18,g11)
    c: Coincident(g18,g0)
    c: Equal(g18,g17)
    c: DistanceX(g7,g-3) = 22
    c: DistanceY(g7,g-3) = 9.97038
    c: Block(g10)
    c: Distance(g16) = 25
FEATURE [PartDesign::Pocket] Pocket020
  BaseFeature = -> BaseFeature002
  Direction = (0,0,-1)
  Length = 5
  Length2 = 5
  Profile = -> Sketch029
  ReferenceAxis = -> Sketch029 [N_Axis]
  Type = 1
FEATURE [Sketcher::SketchObject] Sketch030
  AttachmentOffset = pos=(0,0,1.5) rot=(0,0,1;0rad)
  ExternalGeometry = -> [Pocket020]
  FullyConstrained = true
  MapMode = 5
  Placement = pos=(0,0,1.5) rot=(0,0,1;0rad)
  Support = -> [XY_Plane013]
  expr: .AttachmentOffset.Base.z = Spreadsheet.h_plate
  sketch-geometry (20):
    g0: LineSegment StartX=101.875 StartY=160 StartZ=0 EndX=101.875 EndY=268.536 EndZ=0
    g1: LineSegment StartX=101.875 StartY=268.536 StartZ=0 EndX=180.166 EndY=295.713 EndZ=0
    g2: LineSegment StartX=180.166 StartY=295.713 StartZ=0 EndX=335.212 EndY=273.3 EndZ=0
    g3: LineSegment StartX=335.212 StartY=273.3 StartZ=0 EndX=335.212 EndY=160 EndZ=0
    g4: LineSegment StartX=335.212 StartY=160 StartZ=0 EndX=101.875 EndY=160 EndZ=0
    g5: LineSegment StartX=116.675 StartY=222.5 StartZ=0 EndX=116.675 EndY=166 EndZ=0
    g6: LineSegment StartX=116.675 StartY=166 StartZ=0 EndX=113.875 EndY=166 EndZ=0
    g7: LineSegment StartX=113.875 StartY=166 StartZ=0 EndX=113.875 EndY=222.5 EndZ=0
    g8: LineSegment StartX=113.875 StartY=222.5 StartZ=0 EndX=116.675 EndY=222.5 EndZ=0
    g9: GeomPoint X=115.275 Y=194.25 Z=0
    g10: LineSegment StartX=139.525 StartY=222.5 StartZ=0 EndX=139.525 EndY=166 EndZ=0
    g11: LineSegment StartX=139.525 StartY=166 StartZ=0 EndX=136.725 EndY=166 EndZ=0
    g12: LineSegment StartX=136.725 StartY=166 StartZ=0 EndX=136.725 EndY=222.5 EndZ=0
    g13: LineSegment StartX=136.725 StartY=222.5 StartZ=0 EndX=139.525 EndY=222.5 EndZ=0
    g14: GeomPoint X=138.125 Y=194.25 Z=0
    g15: LineSegment StartX=155.753 StartY=278.77 StartZ=0 EndX=153.13 EndY=286.328 EndZ=0
    g16: LineSegment StartX=0 StartY=0 StartZ=0 EndX=600 EndY=0 EndZ=0
    g17: LineSegment StartX=600 StartY=0 StartZ=0 EndX=600 EndY=600 EndZ=0
    g18: LineSegment StartX=600 StartY=600 StartZ=0 EndX=0 EndY=600 EndZ=0
    g19: LineSegment StartX=0 StartY=600 StartZ=0 EndX=0 EndY=0 EndZ=0
  constraints (59):
    c: Coincident(g0,g1)
    c: Coincident(g1,g2)
    c: Coincident(g2,g3)
    c: Vertical(g3)
    c: Coincident(g3,g4)
    c: Coincident(g4,g0)
    c: Horizontal(g4)
    c: Coincident(g5,g6)
    c: Coincident(g6,g7)
    c: Coincident(g7,g8)
    c: Coincident(g8,g5)
    c: Vertical(g5)
    c: Vertical(g7)
    c: Horizontal(g6)
    c: Horizontal(g8)
    c: Symmetric(g7,g5,g9)
    c: Coincident(g10,g11)
    c: Coincident(g11,g12)
    c: Coincident(g12,g13)
    c: Coincident(g13,g10)
    c: Vertical(g10)
    c: Vertical(g12)
    c: Horizontal(g11)
    c: Horizontal(g13)
    c: Symmetric(g12,g10,g14)
    c: DistanceX(g9,g14) = 22.85
    c: PointOnObject(g7,g13)
    c: Equal(g7,g10)
    c: Equal(g6,g11)
    c: DistanceX(g8,g8) = 2.8
    c: DistanceY(g7,g7) = 56.5
    c: DistanceY(g3,g-3) = 15
    c: DistanceX(g-3,g3) = 8
    c: DistanceY(g0,g6) = 6
    c: DistanceX(g0,g6) = 12
    c: DistanceY(g-5,g1) = 6
    c: DistanceX(g1,g-5) = 0
    c: Coincident(g15,g-6)
    c: PointOnObject(g15,g1)
    c: Perpendicular(g1,g15)
    c: Distance(g15) = 8
    c: Coincident(g16,g17)
    c: Coincident(g17,g18)
    c: Coincident(g18,g19)
    c: Coincident(g19,g16)
    c: Horizontal(g16)
    c: Horizontal(g18)
    c: Vertical(g17)
    c: Vertical(g19)
    c: Distance(g17,g19) = 600
    c: Distance(g16,g18) = 600
    c: Coincident(g16,g-1)
    c: Block(g3)
    c: Block(g2)
    c: Block(g1)
    c: Block(g12)
    c: Vertical(g0)
    c: DistanceY(g-7,g2) = 8
    c: DistanceX(g10,g-4) = 45
FEATURE [PartDesign::Pocket] Pocket021
  BaseFeature = -> Pocket020
  Direction = (0,0,-1)
  Length = 5
  Length2 = 5
  Profile = -> Sketch030
  ReferenceAxis = -> Sketch030 [N_Axis]
  Type = 1
FEATURE [Sketcher::SketchObject] Sketch031
  AttachmentOffset = pos=(0,0,1.5) rot=(0,0,1;0rad)
  ExternalGeometry = -> [Sketch030]
  FullyConstrained = true
  MapMode = 5
  Placement = pos=(0,0,1.5) rot=(0,0,1;0rad)
  Support = -> [XY_Plane013]
  expr: .AttachmentOffset.Base.z = Spreadsheet.h_plate
  expr: Constraints[39] = Spreadsheet.d_wall_out
  sketch-geometry (16):
    g0: LineSegment StartX=101.875 StartY=160 StartZ=0 EndX=101.875 EndY=268.536 EndZ=0
    g1: LineSegment StartX=101.875 StartY=268.536 StartZ=0 EndX=180.166 EndY=295.713 EndZ=0
    g2: LineSegment StartX=180.166 StartY=295.713 StartZ=0 EndX=335.212 EndY=273.3 EndZ=0
    g3: LineSegment StartX=335.212 StartY=273.3 StartZ=0 EndX=335.212 EndY=160 EndZ=0
    g4: LineSegment StartX=335.212 StartY=160 StartZ=0 EndX=101.875 EndY=160 EndZ=0
    g5: LineSegment StartX=103.875 StartY=162 StartZ=0 EndX=103.875 EndY=267.23 EndZ=0
    g6: LineSegment StartX=103.875 StartY=267.23 StartZ=0 EndX=180.166 EndY=293.713 EndZ=0
    g7: LineSegment StartX=180.166 StartY=293.713 StartZ=0 EndX=333.212 EndY=271.589 EndZ=0
    g8: LineSegment StartX=333.212 StartY=271.589 StartZ=0 EndX=333.212 EndY=162 EndZ=0
    g9: LineSegment StartX=333.212 StartY=162 StartZ=0 EndX=103.875 EndY=162 EndZ=0
    g10: LineSegment StartX=103.875 StartY=162 StartZ=0 EndX=103.875 EndY=160 EndZ=0
    g11: LineSegment StartX=103.875 StartY=162 StartZ=0 EndX=101.875 EndY=162 EndZ=0
    g12: LineSegment StartX=103.875 StartY=267.23 StartZ=0 EndX=101.875 EndY=267.23 EndZ=0
    g13: LineSegment StartX=180.166 StartY=295.713 StartZ=0 EndX=180.166 EndY=293.713 EndZ=0
    g14: LineSegment StartX=333.212 StartY=271.589 StartZ=0 EndX=335.212 EndY=271.589 EndZ=0
    g15: LineSegment StartX=333.212 StartY=162 StartZ=0 EndX=335.212 EndY=162 EndZ=0
  constraints (42):
    c: Coincident(g-4,g0)
    c: Coincident(g0,g-7)
    c: Coincident(g0,g1)
    c: Coincident(g1,g-7)
    c: Coincident(g1,g2)
    c: Coincident(g2,g-6)
    c: Coincident(g2,g3)
    c: Coincident(g3,g-5)
    c: Coincident(g3,g4)
    c: Coincident(g4,g0)
    c: Coincident(g5,g6)
    c: Coincident(g5,g9)
    c: Coincident(g6,g7)
    c: Coincident(g7,g8)
    c: Coincident(g8,g9)
    c: Coincident(g10,g5)
    c: PointOnObject(g10,g4)
    c: Vertical(g10)
    c: Coincident(g11,g5)
    c: PointOnObject(g11,g0)
    c: Horizontal(g11)
    c: Equal(g11,g10)
    c: Coincident(g12,g5)
    c: PointOnObject(g12,g0)
    c: Coincident(g13,g1)
    c: Coincident(g6,g13)
    c: Vertical(g13)
    c: Horizontal(g12)
    c: Coincident(g14,g7)
    c: PointOnObject(g14,g3)
    c: Horizontal(g14)
    c: Parallel(g7,g2)
    c: Coincident(g15,g8)
    c: PointOnObject(g15,g3)
    c: Horizontal(g15)
    c: Equal(g15,g14)
    c: Equal(g14,g13)
    c: Equal(g13,g12)
    c: Equal(g12,g11)
    c: DistanceX(g11,g11) = 2
    c: Horizontal(g9)
    c: Parallel(g6,g1)
FEATURE [PartDesign::Pad] Pad029
  BaseFeature = -> Pocket021
  Direction = (0,0,1)
  Length = 15
  Length2 = 10
  Profile = -> Sketch031
  ReferenceAxis = -> Sketch031 [N_Axis]
  Type = 0
  expr: Length = Spreadsheet.h_wall_out
FEATURE [Sketcher::SketchObject] Sketch032
  AttachmentOffset = pos=(0,0,1.5) rot=(0,0,1;0rad)
  FullyConstrained = true
  MapMode = 5
  Placement = pos=(0,0,1.5) rot=(0,0,1;0rad)
  Support = -> [XY_Plane013]
  expr: .AttachmentOffset.Base.z = Spreadsheet.h_plate
  sketch-geometry (6):
    g0: LineSegment StartX=194.05 StartY=191.575 StartZ=0 EndX=333.212 EndY=191.575 EndZ=0
    g1: LineSegment StartX=333.212 StartY=190.8 StartZ=0 EndX=333.212 EndY=192.35 EndZ=0
    g2: LineSegment StartX=333.212 StartY=192.35 StartZ=0 EndX=178.212 EndY=192.35 EndZ=0
    g3: LineSegment StartX=178.212 StartY=192.35 StartZ=0 EndX=178.212 EndY=190.8 EndZ=0
    g4: LineSegment StartX=178.212 StartY=190.8 StartZ=0 EndX=333.212 EndY=190.8 EndZ=0
    g5: GeomPoint X=255.712 Y=191.575 Z=0
  constraints (14):
    c: Coincident(g1,g2)
    c: Coincident(g2,g3)
    c: Coincident(g3,g4)
    c: Coincident(g4,g1)
    c: Vertical(g1)
    c: Vertical(g3)
    c: Horizontal(g2)
    c: Horizontal(g4)
    c: Symmetric(g3,g1,g5)
    c: PointOnObject(g5,g0)
    c: Block(g0)
    c: DistanceY(g3,g3) = 1.55
    c: PointOnObject(g0,g1)
    c: DistanceX(g4,g4) = 155
FEATURE [PartDesign::Pad] Pad030
  BaseFeature = -> Pad029
  Direction = (0,0,1)
  Length = 10
  Length2 = 10
  Profile = -> Sketch032
  ReferenceAxis = -> Sketch032 [N_Axis]
  Type = 3
  UpToFace = -> Pad029 [Face161]
FEATURE [PartDesign::LinearPattern] LinearPattern001
  BaseFeature = -> Pad030
  Direction = -> Y_Axis013
  Length = 57.15
  Mode = 1
  Occurrences = 4
  Offset = 19.05
  Originals = -> [Pad030]
  expr: Offset = Spreadsheet.d_key
FEATURE [PartDesign::Pad] Pad031
  BaseFeature = -> LinearPattern001
  Direction = (-1,0,0)
  Length = 2
  Length2 = 10
  Profile = -> LinearPattern001 [Face167]
  Type = 0
  expr: Length = Spreadsheet.d_wall_out
FEATURE [PartDesign::Pad] Pad032
  BaseFeature = -> Pad031
  Direction = (0,-1,0)
  Length = 10
  Length2 = 10
  Profile = -> Pad031 [Face169]
  Type = 2
FEATURE [Sketcher::SketchObject] Sketch033
  AttachmentOffset = pos=(0,0,1.5) rot=(0,0,1;0rad)
  ExternalGeometry = -> [Pad032]
  FullyConstrained = true
  MapMode = 5
  Placement = pos=(0,0,1.5) rot=(0,0,1;0rad)
  Support = -> [XY_Plane013]
  expr: .AttachmentOffset.Base.z = Spreadsheet.h_plate
  expr: Constraints[11] = Spreadsheet.d_wall_out
  expr: Constraints[25] = Spreadsheet.d_wall_out
  sketch-geometry (10):
    g0: LineSegment StartX=178.212 StartY=230.45 StartZ=0 EndX=103.875 EndY=267.23 EndZ=0
    g1: LineSegment StartX=103.875 StartY=267.23 StartZ=0 EndX=103.875 EndY=264.999 EndZ=0
    g2: LineSegment StartX=103.875 StartY=264.999 StartZ=0 EndX=178.212 EndY=228.219 EndZ=0
    g3: LineSegment StartX=178.212 StartY=228.219 StartZ=0 EndX=178.212 EndY=230.45 EndZ=0
    g4: LineSegment StartX=178.212 StartY=230.45 StartZ=0 EndX=177.326 EndY=228.657 EndZ=0
    g5: LineSegment StartX=176.212 StartY=249.5 StartZ=0 EndX=215.014 EndY=288.675 EndZ=0
    g6: LineSegment StartX=215.014 StartY=288.675 StartZ=0 EndX=217.8 EndY=288.273 EndZ=0
    g7: LineSegment StartX=217.8 StartY=288.273 StartZ=0 EndX=179.027 EndY=249.5 EndZ=0
    g8: LineSegment StartX=179.027 StartY=249.5 StartZ=0 EndX=176.212 EndY=249.5 EndZ=0
    g9: LineSegment StartX=179.027 StartY=249.5 StartZ=0 EndX=177.606 EndY=250.907 EndZ=0
  constraints (27):
    c: Coincident(g-3,g0)
    c: Coincident(g0,g-4)
    c: Coincident(g0,g1)
    c: Vertical(g1)
    c: Coincident(g1,g2)
    c: Coincident(g2,g3)
    c: Coincident(g3,g0)
    c: Vertical(g3)
    c: Coincident(g4,g0)
    c: PointOnObject(g4,g2)
    c: Perpendicular(g2,g4)
    c: Distance(g4) = 2
    c: Equal(g1,g3)
    c: Coincident(g-5,g5)
    c: PointOnObject(g5,g-6)
    c: Coincident(g5,g6)
    c: PointOnObject(g6,g-6)
    c: Coincident(g6,g7)
    c: PointOnObject(g7,g-5)
    c: Coincident(g7,g8)
    c: Coincident(g8,g5)
    c: Equal(g8,g6)
    c: Coincident(g9,g7)
    c: PointOnObject(g9,g5)
    c: Perpendicular(g5,g9)
    c: Distance(g9) = 2
    c: Angle(g-1,g7) = 0.785398
FEATURE [PartDesign::Pad] Pad033
  BaseFeature = -> Pad032
  Direction = (0,0,1)
  Length = 8
  Length2 = 10
  Profile = -> Sketch033
  ReferenceAxis = -> Sketch033 [N_Axis]
  Type = 0
  expr: Length = Spreadsheet.h_wall_in
FEATURE [PartDesign::Pocket] Pocket022
  BaseFeature = -> Pad033
  Direction = (0,0,-1)
  Length = 0
  Length2 = 5
  Profile = -> Pad033 [Face201]
  Type = 3
  UpToFace = -> Pad033 [Face202]
FEATURE [PartDesign::Pocket] Pocket023
  BaseFeature = -> Pocket022
  Direction = (0,0,1)
  Length = 0.2
  Length2 = 5
  Profile = -> Pocket022 [Face1]
  Type = 0
FEATURE [Sketcher::SketchObject] Sketch034
  ExternalGeometry = -> [Pocket023]
  FullyConstrained = false
  MapMode = 5
  Placement = pos=(0,0,0.2) rot=(1,0,0;3.14159rad)
  Support = -> [Pocket023]
  sketch-geometry (8):
    g0: LineSegment StartX=222.758 StartY=-249.5 StartZ=0 EndX=222.758 EndY=-268.032 EndZ=0
    g1: LineSegment StartX=222.758 StartY=-268.032 StartZ=0 EndX=240.883 EndY=-268.032 EndZ=0
    g2: LineSegment StartX=240.883 StartY=-268.032 StartZ=0 EndX=240.883 EndY=-249.5 EndZ=0
    g3: LineSegment StartX=240.883 StartY=-249.5 StartZ=0 EndX=222.758 EndY=-249.5 EndZ=0
    g4: LineSegment StartX=73.3224 StartY=-133.323 StartZ=0 EndX=73.3224 EndY=-375.955 EndZ=0
    g5: LineSegment StartX=73.3224 StartY=-375.955 StartZ=0 EndX=516.325 EndY=-375.955 EndZ=0
    g6: LineSegment StartX=516.325 StartY=-375.955 StartZ=0 EndX=516.325 EndY=-133.323 EndZ=0
    g7: LineSegment StartX=516.325 StartY=-133.323 StartZ=0 EndX=73.3224 EndY=-133.323 EndZ=0
  constraints (17):
    c: Coincident(g0,g1)
    c: Coincident(g1,g2)
    c: Coincident(g2,g3)
    c: Coincident(g3,g0)
    c: Vertical(g0)
    c: Vertical(g2)
    c: Horizontal(g1)
    c: Horizontal(g3)
    c: PointOnObject(g0,g-4)
    c: Coincident(g4,g5)
    c: Coincident(g5,g6)
    c: Coincident(g6,g7)
    c: Coincident(g7,g4)
    c: Vertical(g4)
    c: Vertical(g6)
    c: Horizontal(g5)
    c: Horizontal(g7)
FEATURE [PartDesign::Pocket] Pocket024
  BaseFeature = -> Pocket023
  Direction = (0,0,1)
  Length = 5
  Length2 = 5
  Profile = -> Sketch034
  ReferenceAxis = -> Sketch034 [N_Axis]
  Type = 1
FEATURE [PartDesign::Body] Body003  label="plate_right_v2"
  BaseFeature = -> baseplate_right_v004_solid001
  Group = -> [BaseFeature002,Sketch029,Pocket020,Sketch030,Pocket021,Sketch031,Pad029,Sketch032,Pad030,LinearPattern001,Pad031,Pad032,Sketch033,Pad033,Pocket022,Pocket023,Sketch034,Pocket024]
  Origin = -> Origin013
  Tip = -> Pocket023
FEATURE [App::Part] switch_plate
  Group = -> [LCS_0003,baseplate_left,Body_3,baseplate_left001,baseplate_left001001,baseplate_left001001_solid,plate_right,baseplate_right,baseplate_right001001,baseplate_right001,baseplate_right001001_solid,Body003,baseplate_right_v004_solid001]
  Origin = -> Origin011
FEATURE [App::DocumentObjectGroup] Parts
  Group = -> [Part_1,Part_2,switch_plate]
